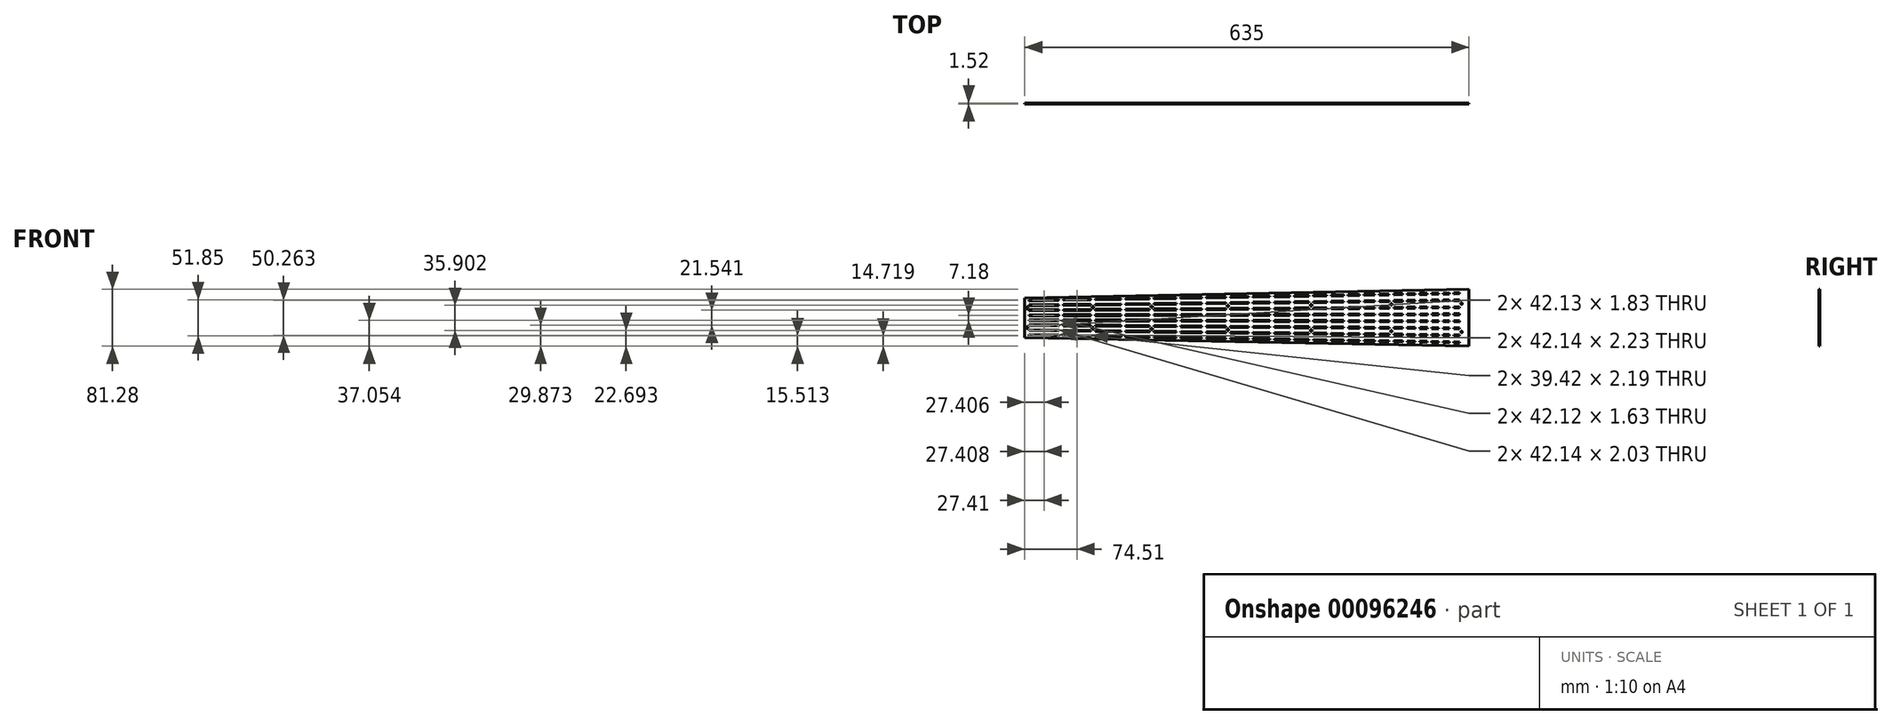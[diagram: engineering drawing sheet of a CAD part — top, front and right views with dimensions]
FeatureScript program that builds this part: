
annotation { "Feature Type Name" : "Feature", "Feature Type Description" : "" }
export const myFeature = defineFeature(function(context is Context, id is Id, definition is map)
    precondition{}
    {
        {
            var Q0;
            Q0=qCreatedBy(makeId("Front.planeOp"),FACE);
            var sketch = newSketch(context, id + "F0", { "sketchPlane" : qUnion([Q0])});
            skLineSegment(sketch, "E0", {"start": v(0, 3.52) * mm, "end": v(646.57, -7.37) * mm, "construction": true});
            skLineSegment(sketch, "E1", {"start": v(0, 4.29) * mm, "end": v(642.9, -6.54) * mm, "construction": true});
            skLineSegment(sketch, "E2", {"start": v(6.35, 3.42) * mm, "end": v(6.36, 4.18) * mm});
            skLineSegment(sketch, "E3", {"start": v(6.36, 4.18) * mm, "end": v(48.48, 3.47) * mm});
            skLineSegment(sketch, "E4", {"start": v(48.48, 3.47) * mm, "end": v(48.46, 2.7) * mm});
            skLineSegment(sketch, "E5", {"start": v(54.81, 2.6) * mm, "end": v(54.83, 3.36) * mm});
            skLineSegment(sketch, "E6", {"start": v(54.83, 3.36) * mm, "end": v(94.22, 2.7) * mm});
            skLineSegment(sketch, "E7", {"start": v(94.22, 2.7) * mm, "end": v(94.2, 1.94) * mm});
            skLineSegment(sketch, "E8", {"start": v(100.56, 1.83) * mm, "end": v(100.57, 2.6) * mm});
            skLineSegment(sketch, "E9", {"start": v(100.57, 2.6) * mm, "end": v(137.4, 1.97) * mm});
            skLineSegment(sketch, "E10", {"start": v(137.4, 1.97) * mm, "end": v(137.38, 1.21) * mm});
            skLineSegment(sketch, "E11", {"start": v(143.73, 1.1) * mm, "end": v(143.74, 1.87) * mm});
            skLineSegment(sketch, "E12", {"start": v(143.74, 1.87) * mm, "end": v(178.14, 1.29) * mm});
            skLineSegment(sketch, "E13", {"start": v(178.14, 1.29) * mm, "end": v(178.13, 0.52) * mm});
            skLineSegment(sketch, "E14", {"start": v(184.48, 0.42) * mm, "end": v(184.49, 1.18) * mm});
            skLineSegment(sketch, "E15", {"start": v(184.49, 1.18) * mm, "end": v(216.61, 0.64) * mm, "construction": true});
            skLineSegment(sketch, "E16", {"start": v(216.61, 0.64) * mm, "end": v(216.6, -0.12) * mm});
            skLineSegment(sketch, "E17", {"start": v(222.95, -0.23) * mm, "end": v(222.96, 0.53) * mm});
            skLineSegment(sketch, "E18", {"start": v(222.96, 0.53) * mm, "end": v(252.92, 0.03) * mm});
            skLineSegment(sketch, "E19", {"start": v(252.92, 0.03) * mm, "end": v(252.9, -0.74) * mm});
            skLineSegment(sketch, "E20", {"start": v(259.26, -0.84) * mm, "end": v(259.27, -0.08) * mm});
            skLineSegment(sketch, "E21", {"start": v(259.27, -0.08) * mm, "end": v(287.19, -0.55) * mm});
            skLineSegment(sketch, "E22", {"start": v(287.19, -0.55) * mm, "end": v(287.18, -1.31) * mm});
            skLineSegment(sketch, "E23", {"start": v(293.52, -1.42) * mm, "end": v(293.54, -0.66) * mm});
            skLineSegment(sketch, "E24", {"start": v(293.54, -0.66) * mm, "end": v(319.53, -1.1) * mm});
            skLineSegment(sketch, "E25", {"start": v(319.53, -1.1) * mm, "end": v(319.52, -1.86) * mm});
            skLineSegment(sketch, "E26", {"start": v(325.87, -1.96) * mm, "end": v(325.88, -1.2) * mm});
            skLineSegment(sketch, "E27", {"start": v(325.88, -1.2) * mm, "end": v(350.06, -1.6) * mm});
            skLineSegment(sketch, "E28", {"start": v(350.06, -1.6) * mm, "end": v(350.05, -2.37) * mm});
            skLineSegment(sketch, "E29", {"start": v(184.49, 1.18) * mm, "end": v(216.61, 0.64) * mm});
            skLineSegment(sketch, "E30", {"start": v(356.4, -2.48) * mm, "end": v(356.41, -1.72) * mm});
            skLineSegment(sketch, "E31", {"start": v(356.41, -1.72) * mm, "end": v(378.88, -2.1) * mm});
            skLineSegment(sketch, "E32", {"start": v(378.88, -2.1) * mm, "end": v(378.87, -2.86) * mm});
            skLineSegment(sketch, "E33", {"start": v(385.22, -2.96) * mm, "end": v(385.23, -2.2) * mm});
            skLineSegment(sketch, "E34", {"start": v(385.23, -2.2) * mm, "end": v(406.08, -2.55) * mm});
            skLineSegment(sketch, "E35", {"start": v(406.08, -2.55) * mm, "end": v(406.07, -3.32) * mm});
            skLineSegment(sketch, "E36", {"start": v(412.41, -3.42) * mm, "end": v(412.43, -2.66) * mm});
            skLineSegment(sketch, "E37", {"start": v(412.43, -2.66) * mm, "end": v(431.75, -2.99) * mm});
            skLineSegment(sketch, "E38", {"start": v(431.75, -2.99) * mm, "end": v(431.74, -3.75) * mm});
            skLineSegment(sketch, "E39", {"start": v(438.09, -3.85) * mm, "end": v(438.1, -3.1) * mm});
            skLineSegment(sketch, "E40", {"start": v(438.1, -3.1) * mm, "end": v(455.98, -3.4) * mm});
            skLineSegment(sketch, "E41", {"start": v(455.98, -3.4) * mm, "end": v(455.97, -4.16) * mm});
            skLineSegment(sketch, "E42", {"start": v(462.32, -4.26) * mm, "end": v(462.33, -3.5) * mm});
            skLineSegment(sketch, "E43", {"start": v(462.33, -3.5) * mm, "end": v(478.86, -3.78) * mm});
            skLineSegment(sketch, "E44", {"start": v(478.86, -3.78) * mm, "end": v(478.84, -4.54) * mm});
            skLineSegment(sketch, "E45", {"start": v(485.2, -4.65) * mm, "end": v(485.2, -3.89) * mm});
            skLineSegment(sketch, "E46", {"start": v(485.2, -3.89) * mm, "end": v(500.44, -4.14) * mm});
            skLineSegment(sketch, "E47", {"start": v(500.44, -4.14) * mm, "end": v(500.43, -4.9) * mm});
            skLineSegment(sketch, "E48", {"start": v(506.78, -5.01) * mm, "end": v(506.8, -4.25) * mm});
            skLineSegment(sketch, "E49", {"start": v(506.8, -4.25) * mm, "end": v(520.82, -4.49) * mm});
            skLineSegment(sketch, "E50", {"start": v(520.82, -4.49) * mm, "end": v(520.8, -5.25) * mm});
            skLineSegment(sketch, "E51", {"start": v(527.16, -5.35) * mm, "end": v(527.17, -4.6) * mm});
            skLineSegment(sketch, "E52", {"start": v(527.17, -4.6) * mm, "end": v(540.05, -4.8) * mm});
            skLineSegment(sketch, "E53", {"start": v(540.05, -4.8) * mm, "end": v(540.04, -5.57) * mm});
            skLineSegment(sketch, "E54", {"start": v(546.39, -5.68) * mm, "end": v(546.4, -4.92) * mm});
            skLineSegment(sketch, "E55", {"start": v(546.4, -4.92) * mm, "end": v(558.2, -5.12) * mm});
            skLineSegment(sketch, "E56", {"start": v(558.2, -5.12) * mm, "end": v(558.2, -5.88) * mm});
            skLineSegment(sketch, "E57", {"start": v(564.54, -5.98) * mm, "end": v(564.55, -5.22) * mm});
            skLineSegment(sketch, "E58", {"start": v(564.55, -5.22) * mm, "end": v(575.34, -5.4) * mm});
            skLineSegment(sketch, "E59", {"start": v(575.34, -5.4) * mm, "end": v(575.33, -6.17) * mm});
            skLineSegment(sketch, "E60", {"start": v(581.68, -6.27) * mm, "end": v(581.69, -5.51) * mm});
            skLineSegment(sketch, "E61", {"start": v(581.69, -5.51) * mm, "end": v(591.51, -5.68) * mm});
            skLineSegment(sketch, "E62", {"start": v(591.51, -5.68) * mm, "end": v(591.5, -6.44) * mm});
            skLineSegment(sketch, "E63", {"start": v(597.85, -6.55) * mm, "end": v(597.86, -5.78) * mm});
            skLineSegment(sketch, "E64", {"start": v(597.86, -5.78) * mm, "end": v(606.78, -5.93) * mm});
            skLineSegment(sketch, "E65", {"start": v(606.78, -5.93) * mm, "end": v(606.76, -6.7) * mm});
            skLineSegment(sketch, "E66", {"start": v(613.11, -6.8) * mm, "end": v(613.13, -6.04) * mm});
            skLineSegment(sketch, "E67", {"start": v(613.13, -6.04) * mm, "end": v(621.19, -6.18) * mm});
            skLineSegment(sketch, "E68", {"start": v(621.19, -6.18) * mm, "end": v(621.17, -6.94) * mm});
            skLineSegment(sketch, "E69.MirrorCS", {"start": v(184.48, 0.42) * mm, "end": v(184.46, -0.34) * mm});
            skLineSegment(sketch, "E70.MirrorCS", {"start": v(606.75, -7.46) * mm, "end": v(606.76, -6.7) * mm});
            skLineSegment(sketch, "E71.MirrorCS", {"start": v(222.95, -0.23) * mm, "end": v(222.94, -1) * mm});
            skLineSegment(sketch, "E72.MirrorCS", {"start": v(558.18, -6.64) * mm, "end": v(558.2, -5.88) * mm});
            skLineSegment(sketch, "E73.MirrorCS", {"start": v(216.59, -0.89) * mm, "end": v(216.6, -0.12) * mm});
            skLineSegment(sketch, "E74.MirrorCS", {"start": v(293.52, -1.42) * mm, "end": v(293.51, -2.18) * mm});
            skLineSegment(sketch, "E75.MirrorCS", {"start": v(94.2, 1.18) * mm, "end": v(94.2, 1.94) * mm});
            skLineSegment(sketch, "E76.MirrorCS", {"start": v(48.45, 1.95) * mm, "end": v(48.46, 2.7) * mm});
            skLineSegment(sketch, "E77.MirrorCS", {"start": v(613.11, -6.8) * mm, "end": v(613.1, -7.56) * mm});
            skLineSegment(sketch, "E78.MirrorCS", {"start": v(597.85, -6.55) * mm, "end": v(597.84, -7.3) * mm});
            skLineSegment(sketch, "E79.MirrorCS", {"start": v(325.87, -1.96) * mm, "end": v(325.86, -2.73) * mm});
            skLineSegment(sketch, "E80.MirrorCS", {"start": v(581.68, -6.27) * mm, "end": v(581.66, -7.03) * mm});
            skLineSegment(sketch, "E81.MirrorCS", {"start": v(478.83, -5.3) * mm, "end": v(478.84, -4.54) * mm});
            skLineSegment(sketch, "E82.MirrorCS", {"start": v(406.05, -4.08) * mm, "end": v(406.07, -3.32) * mm});
            skLineSegment(sketch, "E83.MirrorCS", {"start": v(591.49, -7.2) * mm, "end": v(591.5, -6.44) * mm});
            skLineSegment(sketch, "E84.MirrorCS", {"start": v(485.2, -4.65) * mm, "end": v(485.18, -5.4) * mm});
            skLineSegment(sketch, "E85.MirrorCS", {"start": v(581.66, -7.03) * mm, "end": v(591.49, -7.2) * mm});
            skLineSegment(sketch, "E86.MirrorCS", {"start": v(520.8, -6) * mm, "end": v(520.8, -5.25) * mm});
            skLineSegment(sketch, "E87.MirrorCS", {"start": v(319.5, -2.62) * mm, "end": v(319.52, -1.86) * mm});
            skLineSegment(sketch, "E88.MirrorCS", {"start": v(455.96, -4.92) * mm, "end": v(455.97, -4.16) * mm});
            skLineSegment(sketch, "E89.MirrorCS", {"start": v(564.54, -5.98) * mm, "end": v(564.53, -6.75) * mm});
            skLineSegment(sketch, "E90.MirrorCS", {"start": v(385.22, -2.96) * mm, "end": v(385.2, -3.73) * mm});
            skLineSegment(sketch, "E91.MirrorCS", {"start": v(378.85, -3.62) * mm, "end": v(378.87, -2.86) * mm});
            skLineSegment(sketch, "E92.MirrorCS", {"start": v(506.78, -5.01) * mm, "end": v(506.77, -5.77) * mm});
            skLineSegment(sketch, "E93.MirrorCS", {"start": v(597.84, -7.3) * mm, "end": v(606.75, -7.46) * mm});
            skLineSegment(sketch, "E94.MirrorCS", {"start": v(546.37, -6.44) * mm, "end": v(558.18, -6.64) * mm});
            skLineSegment(sketch, "E95.MirrorCS", {"start": v(143.73, 1.1) * mm, "end": v(143.72, 0.34) * mm});
            skLineSegment(sketch, "E96.MirrorCS", {"start": v(137.37, 0.45) * mm, "end": v(137.38, 1.21) * mm});
            skLineSegment(sketch, "E97.MirrorCS", {"start": v(100.56, 1.83) * mm, "end": v(100.54, 1.07) * mm});
            skLineSegment(sketch, "E98.MirrorCS", {"start": v(54.81, 2.6) * mm, "end": v(54.8, 1.84) * mm});
            skLineSegment(sketch, "E99.MirrorCS", {"start": v(6.35, 3.42) * mm, "end": v(6.34, 2.66) * mm});
            skLineSegment(sketch, "E100.MirrorCS", {"start": v(178.11, -0.24) * mm, "end": v(178.13, 0.52) * mm});
            skLineSegment(sketch, "E101.MirrorCS", {"start": v(431.73, -4.5) * mm, "end": v(431.74, -3.75) * mm});
            skLineSegment(sketch, "E102.MirrorCS", {"start": v(546.39, -5.68) * mm, "end": v(546.37, -6.44) * mm});
            skLineSegment(sketch, "E103.MirrorCS", {"start": v(500.42, -5.67) * mm, "end": v(500.43, -4.9) * mm});
            skLineSegment(sketch, "E104.MirrorCS", {"start": v(287.16, -2.07) * mm, "end": v(287.18, -1.31) * mm});
            skLineSegment(sketch, "E105.MirrorCS", {"start": v(564.53, -6.75) * mm, "end": v(575.31, -6.93) * mm});
            skLineSegment(sketch, "E106.MirrorCS", {"start": v(252.9, -1.5) * mm, "end": v(252.9, -0.74) * mm});
            skLineSegment(sketch, "E107.MirrorCS", {"start": v(613.1, -7.56) * mm, "end": v(621.16, -7.7) * mm});
            skLineSegment(sketch, "E108.MirrorCS", {"start": v(527.16, -5.35) * mm, "end": v(527.14, -6.12) * mm});
            skLineSegment(sketch, "E109.MirrorCS", {"start": v(350.04, -3.13) * mm, "end": v(350.05, -2.37) * mm});
            skLineSegment(sketch, "E110.MirrorCS", {"start": v(412.41, -3.42) * mm, "end": v(412.4, -4.18) * mm});
            skLineSegment(sketch, "E111.MirrorCS", {"start": v(575.31, -6.93) * mm, "end": v(575.33, -6.17) * mm});
            skLineSegment(sketch, "E112.MirrorCS", {"start": v(259.26, -0.84) * mm, "end": v(259.24, -1.6) * mm});
            skLineSegment(sketch, "E113.MirrorCS", {"start": v(621.16, -7.7) * mm, "end": v(621.17, -6.94) * mm});
            skLineSegment(sketch, "E114.MirrorCS", {"start": v(356.4, -2.48) * mm, "end": v(356.39, -3.24) * mm});
            skLineSegment(sketch, "E115.MirrorCS", {"start": v(506.77, -5.77) * mm, "end": v(520.8, -6) * mm});
            skLineSegment(sketch, "E116.MirrorCS", {"start": v(438.09, -3.85) * mm, "end": v(438.08, -4.62) * mm});
            skLineSegment(sketch, "E117.MirrorCS", {"start": v(184.46, -0.34) * mm, "end": v(216.59, -0.89) * mm, "construction": true});
            skLineSegment(sketch, "E118.MirrorCS", {"start": v(462.32, -4.26) * mm, "end": v(462.3, -5.02) * mm});
            skLineSegment(sketch, "E119.MirrorCS", {"start": v(540.03, -6.33) * mm, "end": v(540.04, -5.57) * mm});
            skLineSegment(sketch, "E120.MirrorCS", {"start": v(527.14, -6.12) * mm, "end": v(540.03, -6.33) * mm});
            skLineSegment(sketch, "E121.MirrorCS", {"start": v(222.94, -1) * mm, "end": v(252.9, -1.5) * mm});
            skLineSegment(sketch, "E122.MirrorCS", {"start": v(385.2, -3.73) * mm, "end": v(406.05, -4.08) * mm});
            skLineSegment(sketch, "E123.MirrorCS", {"start": v(293.51, -2.18) * mm, "end": v(319.5, -2.62) * mm});
            skLineSegment(sketch, "E124.MirrorCS", {"start": v(438.08, -4.62) * mm, "end": v(455.96, -4.92) * mm});
            skLineSegment(sketch, "E125.MirrorCS", {"start": v(143.72, 0.34) * mm, "end": v(178.11, -0.24) * mm});
            skLineSegment(sketch, "E126.MirrorCS", {"start": v(54.8, 1.84) * mm, "end": v(94.2, 1.18) * mm});
            skLineSegment(sketch, "E127.MirrorCS", {"start": v(6.34, 2.66) * mm, "end": v(48.45, 1.95) * mm});
            skLineSegment(sketch, "E128.MirrorCS", {"start": v(356.39, -3.24) * mm, "end": v(378.85, -3.62) * mm});
            skLineSegment(sketch, "E129.MirrorCS", {"start": v(259.24, -1.6) * mm, "end": v(287.16, -2.07) * mm});
            skLineSegment(sketch, "E130.MirrorCS", {"start": v(485.18, -5.4) * mm, "end": v(500.42, -5.67) * mm});
            skLineSegment(sketch, "E131.MirrorCS", {"start": v(412.4, -4.18) * mm, "end": v(431.73, -4.5) * mm});
            skLineSegment(sketch, "E132.MirrorCS", {"start": v(184.46, -0.34) * mm, "end": v(216.59, -0.89) * mm});
            skLineSegment(sketch, "E133.MirrorCS", {"start": v(462.3, -5.02) * mm, "end": v(478.83, -5.3) * mm});
            skLineSegment(sketch, "E134.MirrorCS", {"start": v(325.86, -2.73) * mm, "end": v(350.04, -3.13) * mm});
            skLineSegment(sketch, "E135.MirrorCS", {"start": v(100.54, 1.07) * mm, "end": v(137.37, 0.45) * mm});
            skLineSegment(sketch, "E136", {"start": v(-33.04, 0) * mm, "end": v(118.54, 0) * mm, "construction": true});
            skLineSegment(sketch, "E137", {"start": v(0, 10.57) * mm, "end": v(646.61, 2.8) * mm, "construction": true});
            skLineSegment(sketch, "E138", {"start": v(0, 11.33) * mm, "end": v(642.94, 3.6) * mm, "construction": true});
            skLineSegment(sketch, "E139", {"start": v(6.35, 10.5) * mm, "end": v(6.36, 11.26) * mm});
            skLineSegment(sketch, "E140", {"start": v(6.36, 11.26) * mm, "end": v(48.48, 10.75) * mm});
            skLineSegment(sketch, "E141", {"start": v(48.48, 10.75) * mm, "end": v(48.47, 9.99) * mm});
            skLineSegment(sketch, "E142", {"start": v(54.82, 9.91) * mm, "end": v(54.83, 10.68) * mm});
            skLineSegment(sketch, "E143", {"start": v(54.83, 10.68) * mm, "end": v(94.22, 10.2) * mm});
            skLineSegment(sketch, "E144", {"start": v(94.22, 10.2) * mm, "end": v(94.21, 9.44) * mm});
            skLineSegment(sketch, "E145", {"start": v(100.56, 9.36) * mm, "end": v(100.57, 10.12) * mm});
            skLineSegment(sketch, "E146", {"start": v(100.57, 10.12) * mm, "end": v(137.4, 9.68) * mm});
            skLineSegment(sketch, "E147", {"start": v(137.4, 9.68) * mm, "end": v(137.4, 8.92) * mm});
            skLineSegment(sketch, "E148", {"start": v(143.74, 8.84) * mm, "end": v(143.75, 9.6) * mm});
            skLineSegment(sketch, "E149", {"start": v(143.75, 9.6) * mm, "end": v(178.15, 9.2) * mm});
            skLineSegment(sketch, "E150", {"start": v(178.15, 9.2) * mm, "end": v(178.14, 8.43) * mm});
            skLineSegment(sketch, "E151", {"start": v(184.49, 8.35) * mm, "end": v(184.5, 9.12) * mm});
            skLineSegment(sketch, "E152", {"start": v(184.5, 9.12) * mm, "end": v(216.62, 8.73) * mm, "construction": true});
            skLineSegment(sketch, "E153", {"start": v(216.62, 8.73) * mm, "end": v(216.62, 7.97) * mm});
            skLineSegment(sketch, "E154", {"start": v(222.97, 7.9) * mm, "end": v(222.97, 8.65) * mm});
            skLineSegment(sketch, "E155", {"start": v(222.97, 8.65) * mm, "end": v(252.93, 8.3) * mm});
            skLineSegment(sketch, "E156", {"start": v(252.93, 8.3) * mm, "end": v(252.92, 7.53) * mm});
            skLineSegment(sketch, "E157", {"start": v(259.27, 7.45) * mm, "end": v(259.28, 8.22) * mm});
            skLineSegment(sketch, "E158", {"start": v(259.28, 8.22) * mm, "end": v(287.2, 7.88) * mm});
            skLineSegment(sketch, "E159", {"start": v(287.2, 7.88) * mm, "end": v(287.2, 7.12) * mm});
            skLineSegment(sketch, "E160", {"start": v(293.54, 7.04) * mm, "end": v(293.55, 7.8) * mm});
            skLineSegment(sketch, "E161", {"start": v(293.55, 7.8) * mm, "end": v(319.55, 7.5) * mm});
            skLineSegment(sketch, "E162", {"start": v(319.55, 7.5) * mm, "end": v(319.54, 6.73) * mm});
            skLineSegment(sketch, "E163", {"start": v(325.9, 6.65) * mm, "end": v(325.9, 7.41) * mm});
            skLineSegment(sketch, "E164", {"start": v(325.9, 7.41) * mm, "end": v(350.08, 7.12) * mm});
            skLineSegment(sketch, "E165", {"start": v(350.08, 7.12) * mm, "end": v(350.07, 6.36) * mm});
            skLineSegment(sketch, "E166", {"start": v(184.5, 9.12) * mm, "end": v(216.62, 8.73) * mm});
            skLineSegment(sketch, "E167", {"start": v(356.42, 6.28) * mm, "end": v(356.43, 7.05) * mm});
            skLineSegment(sketch, "E168", {"start": v(356.43, 7.05) * mm, "end": v(378.9, 6.78) * mm});
            skLineSegment(sketch, "E169", {"start": v(378.9, 6.78) * mm, "end": v(378.9, 6.01) * mm});
            skLineSegment(sketch, "E170", {"start": v(385.24, 5.94) * mm, "end": v(385.25, 6.7) * mm});
            skLineSegment(sketch, "E171", {"start": v(385.25, 6.7) * mm, "end": v(406.1, 6.45) * mm});
            skLineSegment(sketch, "E172", {"start": v(406.1, 6.45) * mm, "end": v(406.1, 5.69) * mm});
            skLineSegment(sketch, "E173", {"start": v(412.44, 5.61) * mm, "end": v(412.45, 6.37) * mm});
            skLineSegment(sketch, "E174", {"start": v(412.45, 6.37) * mm, "end": v(431.78, 6.14) * mm});
            skLineSegment(sketch, "E175", {"start": v(431.78, 6.14) * mm, "end": v(431.77, 5.38) * mm});
            skLineSegment(sketch, "E176", {"start": v(438.12, 5.3) * mm, "end": v(438.13, 6.06) * mm});
            skLineSegment(sketch, "E177", {"start": v(438.13, 6.06) * mm, "end": v(456.01, 5.85) * mm});
            skLineSegment(sketch, "E178", {"start": v(456.01, 5.85) * mm, "end": v(456, 5.09) * mm});
            skLineSegment(sketch, "E179", {"start": v(462.35, 5.01) * mm, "end": v(462.36, 5.77) * mm});
            skLineSegment(sketch, "E180", {"start": v(462.36, 5.77) * mm, "end": v(478.88, 5.57) * mm});
            skLineSegment(sketch, "E181", {"start": v(478.88, 5.57) * mm, "end": v(478.88, 4.81) * mm});
            skLineSegment(sketch, "E182", {"start": v(485.23, 4.74) * mm, "end": v(485.23, 5.5) * mm});
            skLineSegment(sketch, "E183", {"start": v(485.23, 5.5) * mm, "end": v(500.47, 5.31) * mm});
            skLineSegment(sketch, "E184", {"start": v(500.47, 5.31) * mm, "end": v(500.46, 4.55) * mm});
            skLineSegment(sketch, "E185", {"start": v(506.81, 4.48) * mm, "end": v(506.82, 5.24) * mm});
            skLineSegment(sketch, "E186", {"start": v(506.82, 5.24) * mm, "end": v(520.85, 5.07) * mm});
            skLineSegment(sketch, "E187", {"start": v(520.85, 5.07) * mm, "end": v(520.84, 4.3) * mm});
            skLineSegment(sketch, "E188", {"start": v(527.2, 4.23) * mm, "end": v(527.2, 5) * mm});
            skLineSegment(sketch, "E189", {"start": v(527.2, 5) * mm, "end": v(540.09, 4.84) * mm});
            skLineSegment(sketch, "E190", {"start": v(540.09, 4.84) * mm, "end": v(540.08, 4.08) * mm});
            skLineSegment(sketch, "E191", {"start": v(546.43, 4) * mm, "end": v(546.43, 4.76) * mm});
            skLineSegment(sketch, "E192", {"start": v(546.43, 4.76) * mm, "end": v(558.24, 4.62) * mm});
            skLineSegment(sketch, "E193", {"start": v(558.24, 4.62) * mm, "end": v(558.23, 3.86) * mm});
            skLineSegment(sketch, "E194", {"start": v(564.58, 3.78) * mm, "end": v(564.59, 4.54) * mm});
            skLineSegment(sketch, "E195", {"start": v(564.59, 4.54) * mm, "end": v(575.38, 4.41) * mm});
            skLineSegment(sketch, "E196", {"start": v(575.38, 4.41) * mm, "end": v(575.37, 3.65) * mm});
            skLineSegment(sketch, "E197", {"start": v(581.72, 3.57) * mm, "end": v(581.73, 4.34) * mm});
            skLineSegment(sketch, "E198", {"start": v(581.73, 4.34) * mm, "end": v(591.55, 4.22) * mm});
            skLineSegment(sketch, "E199", {"start": v(591.55, 4.22) * mm, "end": v(591.54, 3.46) * mm});
            skLineSegment(sketch, "E200", {"start": v(597.9, 3.38) * mm, "end": v(597.9, 4.14) * mm});
            skLineSegment(sketch, "E201", {"start": v(597.9, 4.14) * mm, "end": v(606.82, 4.03) * mm});
            skLineSegment(sketch, "E202", {"start": v(606.82, 4.03) * mm, "end": v(606.8, 3.27) * mm});
            skLineSegment(sketch, "E203", {"start": v(613.16, 3.2) * mm, "end": v(613.16, 3.96) * mm});
            skLineSegment(sketch, "E204", {"start": v(613.16, 3.96) * mm, "end": v(621.23, 3.86) * mm});
            skLineSegment(sketch, "E205", {"start": v(621.23, 3.86) * mm, "end": v(621.22, 3.1) * mm});
            skLineSegment(sketch, "E206.MirrorCS", {"start": v(184.49, 8.35) * mm, "end": v(184.48, 7.6) * mm});
            skLineSegment(sketch, "E207.MirrorCS", {"start": v(606.8, 2.51) * mm, "end": v(606.8, 3.27) * mm});
            skLineSegment(sketch, "E208.MirrorCS", {"start": v(222.97, 7.9) * mm, "end": v(222.96, 7.13) * mm});
            skLineSegment(sketch, "E209.MirrorCS", {"start": v(558.22, 3.1) * mm, "end": v(558.23, 3.86) * mm});
            skLineSegment(sketch, "E210.MirrorCS", {"start": v(216.6, 7.2) * mm, "end": v(216.62, 7.97) * mm});
            skLineSegment(sketch, "E211.MirrorCS", {"start": v(293.54, 7.04) * mm, "end": v(293.54, 6.28) * mm});
            skLineSegment(sketch, "E212.MirrorCS", {"start": v(94.2, 8.68) * mm, "end": v(94.21, 9.44) * mm});
            skLineSegment(sketch, "E213.MirrorCS", {"start": v(48.46, 9.23) * mm, "end": v(48.47, 9.99) * mm});
            skLineSegment(sketch, "E214.MirrorCS", {"start": v(613.16, 3.2) * mm, "end": v(613.15, 2.43) * mm});
            skLineSegment(sketch, "E215.MirrorCS", {"start": v(597.9, 3.38) * mm, "end": v(597.88, 2.62) * mm});
            skLineSegment(sketch, "E216.MirrorCS", {"start": v(325.9, 6.65) * mm, "end": v(325.88, 5.9) * mm});
            skLineSegment(sketch, "E217.MirrorCS", {"start": v(581.72, 3.57) * mm, "end": v(581.7, 2.81) * mm});
            skLineSegment(sketch, "E218.MirrorCS", {"start": v(478.87, 4.05) * mm, "end": v(478.88, 4.81) * mm});
            skLineSegment(sketch, "E219.MirrorCS", {"start": v(406.08, 4.93) * mm, "end": v(406.1, 5.69) * mm});
            skLineSegment(sketch, "E220.MirrorCS", {"start": v(591.53, 2.7) * mm, "end": v(591.54, 3.46) * mm});
            skLineSegment(sketch, "E221.MirrorCS", {"start": v(485.23, 4.74) * mm, "end": v(485.22, 3.97) * mm});
            skLineSegment(sketch, "E222.MirrorCS", {"start": v(581.7, 2.81) * mm, "end": v(591.53, 2.7) * mm});
            skLineSegment(sketch, "E223.MirrorCS", {"start": v(520.83, 3.55) * mm, "end": v(520.84, 4.3) * mm});
            skLineSegment(sketch, "E224.MirrorCS", {"start": v(319.53, 5.97) * mm, "end": v(319.54, 6.73) * mm});
            skLineSegment(sketch, "E225.MirrorCS", {"start": v(456, 4.33) * mm, "end": v(456, 5.09) * mm});
            skLineSegment(sketch, "E226.MirrorCS", {"start": v(564.58, 3.78) * mm, "end": v(564.57, 3.02) * mm});
            skLineSegment(sketch, "E227.MirrorCS", {"start": v(385.24, 5.94) * mm, "end": v(385.23, 5.18) * mm});
            skLineSegment(sketch, "E228.MirrorCS", {"start": v(378.88, 5.25) * mm, "end": v(378.9, 6.01) * mm});
            skLineSegment(sketch, "E229.MirrorCS", {"start": v(506.81, 4.48) * mm, "end": v(506.8, 3.71) * mm});
            skLineSegment(sketch, "E230.MirrorCS", {"start": v(597.88, 2.62) * mm, "end": v(606.8, 2.51) * mm});
            skLineSegment(sketch, "E231.MirrorCS", {"start": v(546.42, 3.24) * mm, "end": v(558.22, 3.1) * mm});
            skLineSegment(sketch, "E232.MirrorCS", {"start": v(143.74, 8.84) * mm, "end": v(143.73, 8.08) * mm});
            skLineSegment(sketch, "E233.MirrorCS", {"start": v(137.38, 8.16) * mm, "end": v(137.4, 8.92) * mm});
            skLineSegment(sketch, "E234.MirrorCS", {"start": v(100.56, 9.36) * mm, "end": v(100.55, 8.6) * mm});
            skLineSegment(sketch, "E235.MirrorCS", {"start": v(54.82, 9.91) * mm, "end": v(54.8, 9.15) * mm});
            skLineSegment(sketch, "E236.MirrorCS", {"start": v(6.35, 10.5) * mm, "end": v(6.34, 9.73) * mm});
            skLineSegment(sketch, "E237.MirrorCS", {"start": v(178.13, 7.67) * mm, "end": v(178.14, 8.43) * mm});
            skLineSegment(sketch, "E238.MirrorCS", {"start": v(431.76, 4.62) * mm, "end": v(431.77, 5.38) * mm});
            skLineSegment(sketch, "E239.MirrorCS", {"start": v(546.43, 4) * mm, "end": v(546.42, 3.24) * mm});
            skLineSegment(sketch, "E240.MirrorCS", {"start": v(500.46, 3.8) * mm, "end": v(500.46, 4.55) * mm});
            skLineSegment(sketch, "E241.MirrorCS", {"start": v(287.19, 6.36) * mm, "end": v(287.2, 7.12) * mm});
            skLineSegment(sketch, "E242.MirrorCS", {"start": v(564.57, 3.02) * mm, "end": v(575.36, 2.89) * mm});
            skLineSegment(sketch, "E243.MirrorCS", {"start": v(252.91, 6.77) * mm, "end": v(252.92, 7.53) * mm});
            skLineSegment(sketch, "E244.MirrorCS", {"start": v(613.15, 2.43) * mm, "end": v(621.2, 2.34) * mm});
            skLineSegment(sketch, "E245.MirrorCS", {"start": v(527.2, 4.23) * mm, "end": v(527.18, 3.47) * mm});
            skLineSegment(sketch, "E246.MirrorCS", {"start": v(350.07, 5.6) * mm, "end": v(350.07, 6.36) * mm});
            skLineSegment(sketch, "E247.MirrorCS", {"start": v(412.44, 5.61) * mm, "end": v(412.43, 4.85) * mm});
            skLineSegment(sketch, "E248.MirrorCS", {"start": v(575.36, 2.89) * mm, "end": v(575.37, 3.65) * mm});
            skLineSegment(sketch, "E249.MirrorCS", {"start": v(259.27, 7.45) * mm, "end": v(259.26, 6.7) * mm});
            skLineSegment(sketch, "E250.MirrorCS", {"start": v(621.2, 2.34) * mm, "end": v(621.22, 3.1) * mm});
            skLineSegment(sketch, "E251.MirrorCS", {"start": v(356.42, 6.28) * mm, "end": v(356.42, 5.52) * mm});
            skLineSegment(sketch, "E252.MirrorCS", {"start": v(506.8, 3.71) * mm, "end": v(520.83, 3.55) * mm});
            skLineSegment(sketch, "E253.MirrorCS", {"start": v(438.12, 5.3) * mm, "end": v(438.1, 4.54) * mm});
            skLineSegment(sketch, "E254.MirrorCS", {"start": v(184.48, 7.6) * mm, "end": v(216.6, 7.2) * mm, "construction": true});
            skLineSegment(sketch, "E255.MirrorCS", {"start": v(462.35, 5.01) * mm, "end": v(462.34, 4.25) * mm});
            skLineSegment(sketch, "E256.MirrorCS", {"start": v(540.07, 3.31) * mm, "end": v(540.08, 4.08) * mm});
            skLineSegment(sketch, "E257.MirrorCS", {"start": v(527.18, 3.47) * mm, "end": v(540.07, 3.31) * mm});
            skLineSegment(sketch, "E258.MirrorCS", {"start": v(222.96, 7.13) * mm, "end": v(252.91, 6.77) * mm});
            skLineSegment(sketch, "E259.MirrorCS", {"start": v(385.23, 5.18) * mm, "end": v(406.08, 4.93) * mm});
            skLineSegment(sketch, "E260.MirrorCS", {"start": v(293.54, 6.28) * mm, "end": v(319.53, 5.97) * mm});
            skLineSegment(sketch, "E261.MirrorCS", {"start": v(438.1, 4.54) * mm, "end": v(456, 4.33) * mm});
            skLineSegment(sketch, "E262.MirrorCS", {"start": v(143.73, 8.08) * mm, "end": v(178.13, 7.67) * mm});
            skLineSegment(sketch, "E263.MirrorCS", {"start": v(54.8, 9.15) * mm, "end": v(94.2, 8.68) * mm});
            skLineSegment(sketch, "E264.MirrorCS", {"start": v(6.34, 9.73) * mm, "end": v(48.46, 9.23) * mm});
            skLineSegment(sketch, "E265.MirrorCS", {"start": v(356.42, 5.52) * mm, "end": v(378.88, 5.25) * mm});
            skLineSegment(sketch, "E266.MirrorCS", {"start": v(259.26, 6.7) * mm, "end": v(287.19, 6.36) * mm});
            skLineSegment(sketch, "E267.MirrorCS", {"start": v(485.22, 3.97) * mm, "end": v(500.46, 3.8) * mm});
            skLineSegment(sketch, "E268.MirrorCS", {"start": v(412.43, 4.85) * mm, "end": v(431.76, 4.62) * mm});
            skLineSegment(sketch, "E269.MirrorCS", {"start": v(184.48, 7.6) * mm, "end": v(216.6, 7.2) * mm});
            skLineSegment(sketch, "E270.MirrorCS", {"start": v(462.34, 4.25) * mm, "end": v(478.87, 4.05) * mm});
            skLineSegment(sketch, "E271.MirrorCS", {"start": v(325.88, 5.9) * mm, "end": v(350.07, 5.6) * mm});
            skLineSegment(sketch, "E272.MirrorCS", {"start": v(100.55, 8.6) * mm, "end": v(137.38, 8.16) * mm});
            skLineSegment(sketch, "E273", {"start": v(0, 17.62) * mm, "end": v(646.64, 12.95) * mm, "construction": true});
            skLineSegment(sketch, "E274", {"start": v(0, 18.38) * mm, "end": v(642.97, 13.74) * mm, "construction": true});
            skLineSegment(sketch, "E275", {"start": v(6.35, 17.58) * mm, "end": v(6.36, 18.34) * mm});
            skLineSegment(sketch, "E276", {"start": v(6.36, 18.34) * mm, "end": v(48.47, 18.03) * mm});
            skLineSegment(sketch, "E277", {"start": v(48.47, 18.03) * mm, "end": v(48.47, 17.27) * mm});
            skLineSegment(sketch, "E278", {"start": v(54.82, 17.23) * mm, "end": v(54.82, 17.99) * mm});
            skLineSegment(sketch, "E279", {"start": v(54.82, 17.99) * mm, "end": v(94.22, 17.7) * mm});
            skLineSegment(sketch, "E280", {"start": v(94.22, 17.7) * mm, "end": v(94.22, 16.94) * mm});
            skLineSegment(sketch, "E281", {"start": v(100.57, 16.9) * mm, "end": v(100.57, 17.66) * mm});
            skLineSegment(sketch, "E282", {"start": v(100.57, 17.66) * mm, "end": v(137.4, 17.4) * mm});
            skLineSegment(sketch, "E283", {"start": v(137.4, 17.4) * mm, "end": v(137.4, 16.63) * mm});
            skLineSegment(sketch, "E284", {"start": v(143.75, 16.58) * mm, "end": v(143.75, 17.35) * mm});
            skLineSegment(sketch, "E285", {"start": v(143.75, 17.35) * mm, "end": v(178.15, 17.1) * mm});
            skLineSegment(sketch, "E286", {"start": v(178.15, 17.1) * mm, "end": v(178.15, 16.34) * mm});
            skLineSegment(sketch, "E287", {"start": v(184.5, 16.29) * mm, "end": v(184.5, 17.05) * mm});
            skLineSegment(sketch, "E288", {"start": v(184.5, 17.05) * mm, "end": v(216.63, 16.82) * mm, "construction": true});
            skLineSegment(sketch, "E289", {"start": v(216.63, 16.82) * mm, "end": v(216.63, 16.06) * mm});
            skLineSegment(sketch, "E290", {"start": v(222.98, 16.01) * mm, "end": v(222.98, 16.77) * mm});
            skLineSegment(sketch, "E291", {"start": v(222.98, 16.77) * mm, "end": v(252.94, 16.56) * mm});
            skLineSegment(sketch, "E292", {"start": v(252.94, 16.56) * mm, "end": v(252.94, 15.8) * mm});
            skLineSegment(sketch, "E293", {"start": v(259.29, 15.75) * mm, "end": v(259.3, 16.51) * mm});
            skLineSegment(sketch, "E294", {"start": v(259.3, 16.51) * mm, "end": v(287.21, 16.31) * mm});
            skLineSegment(sketch, "E295", {"start": v(287.21, 16.31) * mm, "end": v(287.2, 15.55) * mm});
            skLineSegment(sketch, "E296", {"start": v(293.56, 15.5) * mm, "end": v(293.56, 16.26) * mm});
            skLineSegment(sketch, "E297", {"start": v(293.56, 16.26) * mm, "end": v(319.56, 16.08) * mm});
            skLineSegment(sketch, "E298", {"start": v(319.56, 16.08) * mm, "end": v(319.56, 15.31) * mm});
            skLineSegment(sketch, "E299", {"start": v(325.9, 15.27) * mm, "end": v(325.91, 16.03) * mm});
            skLineSegment(sketch, "E300", {"start": v(325.91, 16.03) * mm, "end": v(350.1, 15.86) * mm});
            skLineSegment(sketch, "E301", {"start": v(350.1, 15.86) * mm, "end": v(350.1, 15.1) * mm});
            skLineSegment(sketch, "E302", {"start": v(184.5, 17.05) * mm, "end": v(216.63, 16.82) * mm});
            skLineSegment(sketch, "E303", {"start": v(356.44, 15.05) * mm, "end": v(356.45, 15.81) * mm});
            skLineSegment(sketch, "E304", {"start": v(356.45, 15.81) * mm, "end": v(378.92, 15.65) * mm});
            skLineSegment(sketch, "E305", {"start": v(378.92, 15.65) * mm, "end": v(378.91, 14.89) * mm});
            skLineSegment(sketch, "E306", {"start": v(385.26, 14.84) * mm, "end": v(385.27, 15.6) * mm});
            skLineSegment(sketch, "E307", {"start": v(385.27, 15.6) * mm, "end": v(406.12, 15.45) * mm});
            skLineSegment(sketch, "E308", {"start": v(406.12, 15.45) * mm, "end": v(406.11, 14.7) * mm});
            skLineSegment(sketch, "E309", {"start": v(412.46, 14.64) * mm, "end": v(412.47, 15.4) * mm});
            skLineSegment(sketch, "E310", {"start": v(412.47, 15.4) * mm, "end": v(431.8, 15.27) * mm});
            skLineSegment(sketch, "E311", {"start": v(431.8, 15.27) * mm, "end": v(431.79, 14.5) * mm});
            skLineSegment(sketch, "E312", {"start": v(438.14, 14.46) * mm, "end": v(438.14, 15.22) * mm});
            skLineSegment(sketch, "E313", {"start": v(438.14, 15.22) * mm, "end": v(456.03, 15.1) * mm});
            skLineSegment(sketch, "E314", {"start": v(456.03, 15.1) * mm, "end": v(456.02, 14.33) * mm});
            skLineSegment(sketch, "E315", {"start": v(462.37, 14.28) * mm, "end": v(462.38, 15.05) * mm});
            skLineSegment(sketch, "E316", {"start": v(462.38, 15.05) * mm, "end": v(478.9, 14.93) * mm});
            skLineSegment(sketch, "E317", {"start": v(478.9, 14.93) * mm, "end": v(478.9, 14.16) * mm});
            skLineSegment(sketch, "E318", {"start": v(485.25, 14.12) * mm, "end": v(485.25, 14.88) * mm});
            skLineSegment(sketch, "E319", {"start": v(485.25, 14.88) * mm, "end": v(500.5, 14.77) * mm});
            skLineSegment(sketch, "E320", {"start": v(500.5, 14.77) * mm, "end": v(500.49, 14) * mm});
            skLineSegment(sketch, "E321", {"start": v(506.84, 13.96) * mm, "end": v(506.84, 14.73) * mm});
            skLineSegment(sketch, "E322", {"start": v(506.84, 14.73) * mm, "end": v(520.87, 14.62) * mm});
            skLineSegment(sketch, "E323", {"start": v(520.87, 14.62) * mm, "end": v(520.87, 13.86) * mm});
            skLineSegment(sketch, "E324", {"start": v(527.22, 13.82) * mm, "end": v(527.22, 14.58) * mm});
            skLineSegment(sketch, "E325", {"start": v(527.22, 14.58) * mm, "end": v(540.1, 14.48) * mm});
            skLineSegment(sketch, "E326", {"start": v(540.1, 14.48) * mm, "end": v(540.1, 13.72) * mm});
            skLineSegment(sketch, "E327", {"start": v(546.45, 13.68) * mm, "end": v(546.46, 14.44) * mm});
            skLineSegment(sketch, "E328", {"start": v(546.46, 14.44) * mm, "end": v(558.26, 14.35) * mm});
            skLineSegment(sketch, "E329", {"start": v(558.26, 14.35) * mm, "end": v(558.26, 13.6) * mm});
            skLineSegment(sketch, "E330", {"start": v(564.6, 13.55) * mm, "end": v(564.61, 14.3) * mm});
            skLineSegment(sketch, "E331", {"start": v(564.61, 14.3) * mm, "end": v(575.4, 14.23) * mm});
            skLineSegment(sketch, "E332", {"start": v(575.4, 14.23) * mm, "end": v(575.4, 13.47) * mm});
            skLineSegment(sketch, "E333", {"start": v(581.74, 13.42) * mm, "end": v(581.75, 14.18) * mm});
            skLineSegment(sketch, "E334", {"start": v(581.75, 14.18) * mm, "end": v(591.57, 14.11) * mm});
            skLineSegment(sketch, "E335", {"start": v(591.57, 14.11) * mm, "end": v(591.57, 13.35) * mm});
            skLineSegment(sketch, "E336", {"start": v(597.92, 13.3) * mm, "end": v(597.92, 14.07) * mm});
            skLineSegment(sketch, "E337", {"start": v(597.92, 14.07) * mm, "end": v(606.84, 14) * mm});
            skLineSegment(sketch, "E338", {"start": v(606.84, 14) * mm, "end": v(606.83, 13.24) * mm});
            skLineSegment(sketch, "E339", {"start": v(613.18, 13.2) * mm, "end": v(613.19, 13.96) * mm});
            skLineSegment(sketch, "E340", {"start": v(613.19, 13.96) * mm, "end": v(621.25, 13.9) * mm});
            skLineSegment(sketch, "E341", {"start": v(621.25, 13.9) * mm, "end": v(621.24, 13.14) * mm});
            skLineSegment(sketch, "E342.MirrorCS", {"start": v(184.5, 16.29) * mm, "end": v(184.5, 15.53) * mm});
            skLineSegment(sketch, "E343.MirrorCS", {"start": v(606.83, 12.48) * mm, "end": v(606.83, 13.24) * mm});
            skLineSegment(sketch, "E344.MirrorCS", {"start": v(222.98, 16.01) * mm, "end": v(222.97, 15.25) * mm});
            skLineSegment(sketch, "E345.MirrorCS", {"start": v(558.25, 12.83) * mm, "end": v(558.26, 13.6) * mm});
            skLineSegment(sketch, "E346.MirrorCS", {"start": v(216.62, 15.3) * mm, "end": v(216.63, 16.06) * mm});
            skLineSegment(sketch, "E347.MirrorCS", {"start": v(293.56, 15.5) * mm, "end": v(293.55, 14.74) * mm});
            skLineSegment(sketch, "E348.MirrorCS", {"start": v(94.21, 16.18) * mm, "end": v(94.22, 16.94) * mm});
            skLineSegment(sketch, "E349.MirrorCS", {"start": v(48.46, 16.5) * mm, "end": v(48.47, 17.27) * mm});
            skLineSegment(sketch, "E350.MirrorCS", {"start": v(613.18, 13.2) * mm, "end": v(613.18, 12.43) * mm});
            skLineSegment(sketch, "E351.MirrorCS", {"start": v(597.92, 13.3) * mm, "end": v(597.91, 12.54) * mm});
            skLineSegment(sketch, "E352.MirrorCS", {"start": v(325.9, 15.27) * mm, "end": v(325.9, 14.5) * mm});
            skLineSegment(sketch, "E353.MirrorCS", {"start": v(581.74, 13.42) * mm, "end": v(581.74, 12.66) * mm});
            skLineSegment(sketch, "E354.MirrorCS", {"start": v(478.9, 13.4) * mm, "end": v(478.9, 14.16) * mm});
            skLineSegment(sketch, "E355.MirrorCS", {"start": v(406.1, 13.93) * mm, "end": v(406.11, 14.7) * mm});
            skLineSegment(sketch, "E356.MirrorCS", {"start": v(591.56, 12.59) * mm, "end": v(591.57, 13.35) * mm});
            skLineSegment(sketch, "E357.MirrorCS", {"start": v(485.25, 14.12) * mm, "end": v(485.24, 13.36) * mm});
            skLineSegment(sketch, "E358.MirrorCS", {"start": v(581.74, 12.66) * mm, "end": v(591.56, 12.59) * mm});
            skLineSegment(sketch, "E359.MirrorCS", {"start": v(520.86, 13.1) * mm, "end": v(520.87, 13.86) * mm});
            skLineSegment(sketch, "E360.MirrorCS", {"start": v(319.55, 14.55) * mm, "end": v(319.56, 15.31) * mm});
            skLineSegment(sketch, "E361.MirrorCS", {"start": v(456.02, 13.57) * mm, "end": v(456.02, 14.33) * mm});
            skLineSegment(sketch, "E362.MirrorCS", {"start": v(564.6, 13.55) * mm, "end": v(564.6, 12.78) * mm});
            skLineSegment(sketch, "E363.MirrorCS", {"start": v(385.26, 14.84) * mm, "end": v(385.26, 14.08) * mm});
            skLineSegment(sketch, "E364.MirrorCS", {"start": v(378.9, 14.12) * mm, "end": v(378.91, 14.89) * mm});
            skLineSegment(sketch, "E365.MirrorCS", {"start": v(506.84, 13.96) * mm, "end": v(506.83, 13.2) * mm});
            skLineSegment(sketch, "E366.MirrorCS", {"start": v(597.91, 12.54) * mm, "end": v(606.83, 12.48) * mm});
            skLineSegment(sketch, "E367.MirrorCS", {"start": v(546.45, 12.92) * mm, "end": v(558.25, 12.83) * mm});
            skLineSegment(sketch, "E368.MirrorCS", {"start": v(143.75, 16.58) * mm, "end": v(143.74, 15.82) * mm});
            skLineSegment(sketch, "E369.MirrorCS", {"start": v(137.4, 15.87) * mm, "end": v(137.4, 16.63) * mm});
            skLineSegment(sketch, "E370.MirrorCS", {"start": v(100.57, 16.9) * mm, "end": v(100.56, 16.13) * mm});
            skLineSegment(sketch, "E371.MirrorCS", {"start": v(54.82, 17.23) * mm, "end": v(54.81, 16.46) * mm});
            skLineSegment(sketch, "E372.MirrorCS", {"start": v(6.35, 17.58) * mm, "end": v(6.34, 16.81) * mm});
            skLineSegment(sketch, "E373.MirrorCS", {"start": v(178.14, 15.57) * mm, "end": v(178.15, 16.34) * mm});
            skLineSegment(sketch, "E374.MirrorCS", {"start": v(431.78, 13.74) * mm, "end": v(431.79, 14.5) * mm});
            skLineSegment(sketch, "E375.MirrorCS", {"start": v(546.45, 13.68) * mm, "end": v(546.45, 12.92) * mm});
            skLineSegment(sketch, "E376.MirrorCS", {"start": v(500.48, 13.25) * mm, "end": v(500.49, 14) * mm});
            skLineSegment(sketch, "E377.MirrorCS", {"start": v(287.2, 14.79) * mm, "end": v(287.2, 15.55) * mm});
            skLineSegment(sketch, "E378.MirrorCS", {"start": v(564.6, 12.78) * mm, "end": v(575.39, 12.7) * mm});
            skLineSegment(sketch, "E379.MirrorCS", {"start": v(252.93, 15.03) * mm, "end": v(252.94, 15.8) * mm});
            skLineSegment(sketch, "E380.MirrorCS", {"start": v(613.18, 12.43) * mm, "end": v(621.24, 12.38) * mm});
            skLineSegment(sketch, "E381.MirrorCS", {"start": v(527.22, 13.82) * mm, "end": v(527.21, 13.05) * mm});
            skLineSegment(sketch, "E382.MirrorCS", {"start": v(350.09, 14.33) * mm, "end": v(350.1, 15.1) * mm});
            skLineSegment(sketch, "E383.MirrorCS", {"start": v(412.46, 14.64) * mm, "end": v(412.46, 13.88) * mm});
            skLineSegment(sketch, "E384.MirrorCS", {"start": v(575.39, 12.7) * mm, "end": v(575.4, 13.47) * mm});
            skLineSegment(sketch, "E385.MirrorCS", {"start": v(259.29, 15.75) * mm, "end": v(259.28, 14.99) * mm});
            skLineSegment(sketch, "E386.MirrorCS", {"start": v(621.24, 12.38) * mm, "end": v(621.24, 13.14) * mm});
            skLineSegment(sketch, "E387.MirrorCS", {"start": v(356.44, 15.05) * mm, "end": v(356.44, 14.29) * mm});
            skLineSegment(sketch, "E388.MirrorCS", {"start": v(506.83, 13.2) * mm, "end": v(520.86, 13.1) * mm});
            skLineSegment(sketch, "E389.MirrorCS", {"start": v(438.14, 14.46) * mm, "end": v(438.13, 13.7) * mm});
            skLineSegment(sketch, "E390.MirrorCS", {"start": v(184.5, 15.53) * mm, "end": v(216.62, 15.3) * mm, "construction": true});
            skLineSegment(sketch, "E391.MirrorCS", {"start": v(462.37, 14.28) * mm, "end": v(462.37, 13.52) * mm});
            skLineSegment(sketch, "E392.MirrorCS", {"start": v(540.1, 12.96) * mm, "end": v(540.1, 13.72) * mm});
            skLineSegment(sketch, "E393.MirrorCS", {"start": v(527.21, 13.05) * mm, "end": v(540.1, 12.96) * mm});
            skLineSegment(sketch, "E394.MirrorCS", {"start": v(222.97, 15.25) * mm, "end": v(252.93, 15.03) * mm});
            skLineSegment(sketch, "E395.MirrorCS", {"start": v(385.26, 14.08) * mm, "end": v(406.1, 13.93) * mm});
            skLineSegment(sketch, "E396.MirrorCS", {"start": v(293.55, 14.74) * mm, "end": v(319.55, 14.55) * mm});
            skLineSegment(sketch, "E397.MirrorCS", {"start": v(438.13, 13.7) * mm, "end": v(456.02, 13.57) * mm});
            skLineSegment(sketch, "E398.MirrorCS", {"start": v(143.74, 15.82) * mm, "end": v(178.14, 15.57) * mm});
            skLineSegment(sketch, "E399.MirrorCS", {"start": v(54.81, 16.46) * mm, "end": v(94.21, 16.18) * mm});
            skLineSegment(sketch, "E400.MirrorCS", {"start": v(6.34, 16.81) * mm, "end": v(48.46, 16.5) * mm});
            skLineSegment(sketch, "E401.MirrorCS", {"start": v(356.44, 14.29) * mm, "end": v(378.9, 14.12) * mm});
            skLineSegment(sketch, "E402.MirrorCS", {"start": v(259.28, 14.99) * mm, "end": v(287.2, 14.79) * mm});
            skLineSegment(sketch, "E403.MirrorCS", {"start": v(485.24, 13.36) * mm, "end": v(500.48, 13.25) * mm});
            skLineSegment(sketch, "E404.MirrorCS", {"start": v(412.46, 13.88) * mm, "end": v(431.78, 13.74) * mm});
            skLineSegment(sketch, "E405.MirrorCS", {"start": v(184.5, 15.53) * mm, "end": v(216.62, 15.3) * mm});
            skLineSegment(sketch, "E406.MirrorCS", {"start": v(462.37, 13.52) * mm, "end": v(478.9, 13.4) * mm});
            skLineSegment(sketch, "E407.MirrorCS", {"start": v(325.9, 14.5) * mm, "end": v(350.09, 14.33) * mm});
            skLineSegment(sketch, "E408.MirrorCS", {"start": v(100.56, 16.13) * mm, "end": v(137.4, 15.87) * mm});
            skLineSegment(sketch, "E409", {"start": v(0, 24.67) * mm, "end": v(646.66, 23.11) * mm, "construction": true});
            skLineSegment(sketch, "E410", {"start": v(0, 25.43) * mm, "end": v(642.98, 23.88) * mm, "construction": true});
            skLineSegment(sketch, "E411", {"start": v(6.35, 24.65) * mm, "end": v(6.35, 25.42) * mm});
            skLineSegment(sketch, "E412", {"start": v(6.35, 25.42) * mm, "end": v(48.47, 25.32) * mm});
            skLineSegment(sketch, "E413", {"start": v(48.47, 25.32) * mm, "end": v(48.47, 24.55) * mm});
            skLineSegment(sketch, "E414", {"start": v(54.82, 24.54) * mm, "end": v(54.82, 25.3) * mm});
            skLineSegment(sketch, "E415", {"start": v(54.82, 25.3) * mm, "end": v(94.22, 25.2) * mm});
            skLineSegment(sketch, "E416", {"start": v(94.22, 25.2) * mm, "end": v(94.22, 24.44) * mm});
            skLineSegment(sketch, "E417", {"start": v(100.57, 24.43) * mm, "end": v(100.57, 25.19) * mm});
            skLineSegment(sketch, "E418", {"start": v(100.57, 25.19) * mm, "end": v(137.4, 25.1) * mm});
            skLineSegment(sketch, "E419", {"start": v(137.4, 25.1) * mm, "end": v(137.4, 24.34) * mm});
            skLineSegment(sketch, "E420", {"start": v(143.75, 24.32) * mm, "end": v(143.75, 25.09) * mm});
            skLineSegment(sketch, "E421", {"start": v(143.75, 25.09) * mm, "end": v(178.15, 25) * mm});
            skLineSegment(sketch, "E422", {"start": v(178.15, 25) * mm, "end": v(178.15, 24.24) * mm});
            skLineSegment(sketch, "E423", {"start": v(184.5, 24.23) * mm, "end": v(184.5, 24.99) * mm});
            skLineSegment(sketch, "E424", {"start": v(184.5, 24.99) * mm, "end": v(216.63, 24.91) * mm, "construction": true});
            skLineSegment(sketch, "E425", {"start": v(216.63, 24.91) * mm, "end": v(216.63, 24.15) * mm});
            skLineSegment(sketch, "E426", {"start": v(222.98, 24.13) * mm, "end": v(222.98, 24.9) * mm});
            skLineSegment(sketch, "E427", {"start": v(222.98, 24.9) * mm, "end": v(252.94, 24.82) * mm});
            skLineSegment(sketch, "E428", {"start": v(252.94, 24.82) * mm, "end": v(252.94, 24.06) * mm});
            skLineSegment(sketch, "E429", {"start": v(259.3, 24.05) * mm, "end": v(259.3, 24.8) * mm});
            skLineSegment(sketch, "E430", {"start": v(259.3, 24.8) * mm, "end": v(287.22, 24.74) * mm});
            skLineSegment(sketch, "E431", {"start": v(287.22, 24.74) * mm, "end": v(287.22, 23.98) * mm});
            skLineSegment(sketch, "E432", {"start": v(293.57, 23.96) * mm, "end": v(293.57, 24.73) * mm});
            skLineSegment(sketch, "E433", {"start": v(293.57, 24.73) * mm, "end": v(319.57, 24.66) * mm});
            skLineSegment(sketch, "E434", {"start": v(319.57, 24.66) * mm, "end": v(319.56, 23.9) * mm});
            skLineSegment(sketch, "E435", {"start": v(325.91, 23.89) * mm, "end": v(325.92, 24.65) * mm});
            skLineSegment(sketch, "E436", {"start": v(325.92, 24.65) * mm, "end": v(350.1, 24.59) * mm});
            skLineSegment(sketch, "E437", {"start": v(350.1, 24.59) * mm, "end": v(350.1, 23.83) * mm});
            skLineSegment(sketch, "E438", {"start": v(184.5, 24.99) * mm, "end": v(216.63, 24.91) * mm});
            skLineSegment(sketch, "E439", {"start": v(356.45, 23.81) * mm, "end": v(356.45, 24.57) * mm});
            skLineSegment(sketch, "E440", {"start": v(356.45, 24.57) * mm, "end": v(378.92, 24.52) * mm});
            skLineSegment(sketch, "E441", {"start": v(378.92, 24.52) * mm, "end": v(378.92, 23.76) * mm});
            skLineSegment(sketch, "E442", {"start": v(385.27, 23.74) * mm, "end": v(385.27, 24.5) * mm});
            skLineSegment(sketch, "E443", {"start": v(385.27, 24.5) * mm, "end": v(406.12, 24.45) * mm});
            skLineSegment(sketch, "E444", {"start": v(406.12, 24.45) * mm, "end": v(406.12, 23.7) * mm});
            skLineSegment(sketch, "E445", {"start": v(412.47, 23.68) * mm, "end": v(412.47, 24.44) * mm});
            skLineSegment(sketch, "E446", {"start": v(412.47, 24.44) * mm, "end": v(431.8, 24.4) * mm});
            skLineSegment(sketch, "E447", {"start": v(431.8, 24.4) * mm, "end": v(431.8, 23.63) * mm});
            skLineSegment(sketch, "E448", {"start": v(438.15, 23.62) * mm, "end": v(438.15, 24.38) * mm});
            skLineSegment(sketch, "E449", {"start": v(438.15, 24.38) * mm, "end": v(456.04, 24.33) * mm});
            skLineSegment(sketch, "E450", {"start": v(456.04, 24.33) * mm, "end": v(456.03, 23.57) * mm});
            skLineSegment(sketch, "E451", {"start": v(462.38, 23.56) * mm, "end": v(462.39, 24.32) * mm});
            skLineSegment(sketch, "E452", {"start": v(462.39, 24.32) * mm, "end": v(478.91, 24.28) * mm});
            skLineSegment(sketch, "E453", {"start": v(478.91, 24.28) * mm, "end": v(478.9, 23.52) * mm});
            skLineSegment(sketch, "E454", {"start": v(485.26, 23.5) * mm, "end": v(485.26, 24.26) * mm});
            skLineSegment(sketch, "E455", {"start": v(485.26, 24.26) * mm, "end": v(500.5, 24.23) * mm});
            skLineSegment(sketch, "E456", {"start": v(500.5, 24.23) * mm, "end": v(500.5, 23.47) * mm});
            skLineSegment(sketch, "E457", {"start": v(506.85, 23.45) * mm, "end": v(506.85, 24.21) * mm});
            skLineSegment(sketch, "E458", {"start": v(506.85, 24.21) * mm, "end": v(520.88, 24.18) * mm});
            skLineSegment(sketch, "E459", {"start": v(520.88, 24.18) * mm, "end": v(520.88, 23.42) * mm});
            skLineSegment(sketch, "E460", {"start": v(527.23, 23.4) * mm, "end": v(527.23, 24.16) * mm});
            skLineSegment(sketch, "E461", {"start": v(527.23, 24.16) * mm, "end": v(540.12, 24.13) * mm});
            skLineSegment(sketch, "E462", {"start": v(540.12, 24.13) * mm, "end": v(540.11, 23.37) * mm});
            skLineSegment(sketch, "E463", {"start": v(546.46, 23.36) * mm, "end": v(546.47, 24.12) * mm});
            skLineSegment(sketch, "E464", {"start": v(546.47, 24.12) * mm, "end": v(558.27, 24.09) * mm});
            skLineSegment(sketch, "E465", {"start": v(558.27, 24.09) * mm, "end": v(558.27, 23.33) * mm});
            skLineSegment(sketch, "E466", {"start": v(564.62, 23.31) * mm, "end": v(564.62, 24.07) * mm});
            skLineSegment(sketch, "E467", {"start": v(564.62, 24.07) * mm, "end": v(575.4, 24.05) * mm});
            skLineSegment(sketch, "E468", {"start": v(575.4, 24.05) * mm, "end": v(575.4, 23.29) * mm});
            skLineSegment(sketch, "E469", {"start": v(581.76, 23.27) * mm, "end": v(581.76, 24.03) * mm});
            skLineSegment(sketch, "E470", {"start": v(581.76, 24.03) * mm, "end": v(591.58, 24) * mm});
            skLineSegment(sketch, "E471", {"start": v(591.58, 24) * mm, "end": v(591.58, 23.25) * mm});
            skLineSegment(sketch, "E472", {"start": v(597.93, 23.23) * mm, "end": v(597.93, 24) * mm});
            skLineSegment(sketch, "E473", {"start": v(597.93, 24) * mm, "end": v(606.85, 23.97) * mm});
            skLineSegment(sketch, "E474", {"start": v(606.85, 23.97) * mm, "end": v(606.85, 23.2) * mm});
            skLineSegment(sketch, "E475", {"start": v(613.2, 23.2) * mm, "end": v(613.2, 23.96) * mm});
            skLineSegment(sketch, "E476", {"start": v(613.2, 23.96) * mm, "end": v(621.26, 23.94) * mm});
            skLineSegment(sketch, "E477", {"start": v(621.26, 23.94) * mm, "end": v(621.26, 23.18) * mm});
            skLineSegment(sketch, "E478.MirrorCS", {"start": v(184.5, 24.23) * mm, "end": v(184.5, 23.46) * mm});
            skLineSegment(sketch, "E479.MirrorCS", {"start": v(606.85, 22.45) * mm, "end": v(606.85, 23.2) * mm});
            skLineSegment(sketch, "E480.MirrorCS", {"start": v(222.98, 24.13) * mm, "end": v(222.98, 23.37) * mm});
            skLineSegment(sketch, "E481.MirrorCS", {"start": v(558.27, 22.56) * mm, "end": v(558.27, 23.33) * mm});
            skLineSegment(sketch, "E482.MirrorCS", {"start": v(216.63, 23.39) * mm, "end": v(216.63, 24.15) * mm});
            skLineSegment(sketch, "E483.MirrorCS", {"start": v(293.57, 23.96) * mm, "end": v(293.56, 23.2) * mm});
            skLineSegment(sketch, "E484.MirrorCS", {"start": v(94.22, 23.68) * mm, "end": v(94.22, 24.44) * mm});
            skLineSegment(sketch, "E485.MirrorCS", {"start": v(48.47, 23.8) * mm, "end": v(48.47, 24.55) * mm});
            skLineSegment(sketch, "E486.MirrorCS", {"start": v(613.2, 23.2) * mm, "end": v(613.2, 22.43) * mm});
            skLineSegment(sketch, "E487.MirrorCS", {"start": v(597.93, 23.23) * mm, "end": v(597.93, 22.47) * mm});
            skLineSegment(sketch, "E488.MirrorCS", {"start": v(325.91, 23.89) * mm, "end": v(325.91, 23.12) * mm});
            skLineSegment(sketch, "E489.MirrorCS", {"start": v(581.76, 23.27) * mm, "end": v(581.75, 22.5) * mm});
            skLineSegment(sketch, "E490.MirrorCS", {"start": v(478.9, 22.76) * mm, "end": v(478.9, 23.52) * mm});
            skLineSegment(sketch, "E491.MirrorCS", {"start": v(406.12, 22.93) * mm, "end": v(406.12, 23.7) * mm});
            skLineSegment(sketch, "E492.MirrorCS", {"start": v(591.58, 22.48) * mm, "end": v(591.58, 23.25) * mm});
            skLineSegment(sketch, "E493.MirrorCS", {"start": v(485.26, 23.5) * mm, "end": v(485.26, 22.74) * mm});
            skLineSegment(sketch, "E494.MirrorCS", {"start": v(581.75, 22.5) * mm, "end": v(591.58, 22.48) * mm});
            skLineSegment(sketch, "E495.MirrorCS", {"start": v(520.88, 22.65) * mm, "end": v(520.88, 23.42) * mm});
            skLineSegment(sketch, "E496.MirrorCS", {"start": v(319.56, 23.14) * mm, "end": v(319.56, 23.9) * mm});
            skLineSegment(sketch, "E497.MirrorCS", {"start": v(456.03, 22.81) * mm, "end": v(456.03, 23.57) * mm});
            skLineSegment(sketch, "E498.MirrorCS", {"start": v(564.62, 23.31) * mm, "end": v(564.62, 22.55) * mm});
            skLineSegment(sketch, "E499.MirrorCS", {"start": v(385.27, 23.74) * mm, "end": v(385.27, 22.98) * mm});
            skLineSegment(sketch, "E500.MirrorCS", {"start": v(378.92, 23) * mm, "end": v(378.92, 23.76) * mm});
            skLineSegment(sketch, "E501.MirrorCS", {"start": v(506.85, 23.45) * mm, "end": v(506.85, 22.69) * mm});
            skLineSegment(sketch, "E502.MirrorCS", {"start": v(597.93, 22.47) * mm, "end": v(606.85, 22.45) * mm});
            skLineSegment(sketch, "E503.MirrorCS", {"start": v(546.46, 22.6) * mm, "end": v(558.27, 22.56) * mm});
            skLineSegment(sketch, "E504.MirrorCS", {"start": v(143.75, 24.32) * mm, "end": v(143.75, 23.56) * mm});
            skLineSegment(sketch, "E505.MirrorCS", {"start": v(137.4, 23.58) * mm, "end": v(137.4, 24.34) * mm});
            skLineSegment(sketch, "E506.MirrorCS", {"start": v(100.57, 24.43) * mm, "end": v(100.57, 23.67) * mm});
            skLineSegment(sketch, "E507.MirrorCS", {"start": v(54.82, 24.54) * mm, "end": v(54.82, 23.78) * mm});
            skLineSegment(sketch, "E508.MirrorCS", {"start": v(6.35, 24.65) * mm, "end": v(6.35, 23.9) * mm});
            skLineSegment(sketch, "E509.MirrorCS", {"start": v(178.15, 23.48) * mm, "end": v(178.15, 24.24) * mm});
            skLineSegment(sketch, "E510.MirrorCS", {"start": v(431.8, 22.87) * mm, "end": v(431.8, 23.63) * mm});
            skLineSegment(sketch, "E511.MirrorCS", {"start": v(546.46, 23.36) * mm, "end": v(546.46, 22.6) * mm});
            skLineSegment(sketch, "E512.MirrorCS", {"start": v(500.5, 22.7) * mm, "end": v(500.5, 23.47) * mm});
            skLineSegment(sketch, "E513.MirrorCS", {"start": v(287.21, 23.22) * mm, "end": v(287.22, 23.98) * mm});
            skLineSegment(sketch, "E514.MirrorCS", {"start": v(564.62, 22.55) * mm, "end": v(575.4, 22.52) * mm});
            skLineSegment(sketch, "E515.MirrorCS", {"start": v(252.94, 23.3) * mm, "end": v(252.94, 24.06) * mm});
            skLineSegment(sketch, "E516.MirrorCS", {"start": v(613.2, 22.43) * mm, "end": v(621.26, 22.41) * mm});
            skLineSegment(sketch, "E517.MirrorCS", {"start": v(527.23, 23.4) * mm, "end": v(527.23, 22.64) * mm});
            skLineSegment(sketch, "E518.MirrorCS", {"start": v(350.1, 23.07) * mm, "end": v(350.1, 23.83) * mm});
            skLineSegment(sketch, "E519.MirrorCS", {"start": v(412.47, 23.68) * mm, "end": v(412.47, 22.92) * mm});
            skLineSegment(sketch, "E520.MirrorCS", {"start": v(575.4, 22.52) * mm, "end": v(575.4, 23.29) * mm});
            skLineSegment(sketch, "E521.MirrorCS", {"start": v(259.3, 24.05) * mm, "end": v(259.29, 23.28) * mm});
            skLineSegment(sketch, "E522.MirrorCS", {"start": v(621.26, 22.41) * mm, "end": v(621.26, 23.18) * mm});
            skLineSegment(sketch, "E523.MirrorCS", {"start": v(356.45, 23.81) * mm, "end": v(356.45, 23.05) * mm});
            skLineSegment(sketch, "E524.MirrorCS", {"start": v(506.85, 22.69) * mm, "end": v(520.88, 22.65) * mm});
            skLineSegment(sketch, "E525.MirrorCS", {"start": v(438.15, 23.62) * mm, "end": v(438.15, 22.85) * mm});
            skLineSegment(sketch, "E526.MirrorCS", {"start": v(184.5, 23.46) * mm, "end": v(216.63, 23.39) * mm, "construction": true});
            skLineSegment(sketch, "E527.MirrorCS", {"start": v(462.38, 23.56) * mm, "end": v(462.38, 22.8) * mm});
            skLineSegment(sketch, "E528.MirrorCS", {"start": v(540.11, 22.6) * mm, "end": v(540.11, 23.37) * mm});
            skLineSegment(sketch, "E529.MirrorCS", {"start": v(527.23, 22.64) * mm, "end": v(540.11, 22.6) * mm});
            skLineSegment(sketch, "E530.MirrorCS", {"start": v(222.98, 23.37) * mm, "end": v(252.94, 23.3) * mm});
            skLineSegment(sketch, "E531.MirrorCS", {"start": v(385.27, 22.98) * mm, "end": v(406.12, 22.93) * mm});
            skLineSegment(sketch, "E532.MirrorCS", {"start": v(293.56, 23.2) * mm, "end": v(319.56, 23.14) * mm});
            skLineSegment(sketch, "E533.MirrorCS", {"start": v(438.15, 22.85) * mm, "end": v(456.03, 22.81) * mm});
            skLineSegment(sketch, "E534.MirrorCS", {"start": v(143.75, 23.56) * mm, "end": v(178.15, 23.48) * mm});
            skLineSegment(sketch, "E535.MirrorCS", {"start": v(54.82, 23.78) * mm, "end": v(94.22, 23.68) * mm});
            skLineSegment(sketch, "E536.MirrorCS", {"start": v(6.35, 23.9) * mm, "end": v(48.47, 23.8) * mm});
            skLineSegment(sketch, "E537.MirrorCS", {"start": v(356.45, 23.05) * mm, "end": v(378.92, 23) * mm});
            skLineSegment(sketch, "E538.MirrorCS", {"start": v(259.29, 23.28) * mm, "end": v(287.21, 23.22) * mm});
            skLineSegment(sketch, "E539.MirrorCS", {"start": v(485.26, 22.74) * mm, "end": v(500.5, 22.7) * mm});
            skLineSegment(sketch, "E540.MirrorCS", {"start": v(412.47, 22.92) * mm, "end": v(431.8, 22.87) * mm});
            skLineSegment(sketch, "E541.MirrorCS", {"start": v(184.5, 23.46) * mm, "end": v(216.63, 23.39) * mm});
            skLineSegment(sketch, "E542.MirrorCS", {"start": v(462.38, 22.8) * mm, "end": v(478.9, 22.76) * mm});
            skLineSegment(sketch, "E543.MirrorCS", {"start": v(325.91, 23.12) * mm, "end": v(350.1, 23.07) * mm});
            skLineSegment(sketch, "E544.MirrorCS", {"start": v(100.57, 23.67) * mm, "end": v(137.4, 23.58) * mm});
            skLineSegment(sketch, "E545", {"start": v(0, 28.2) * mm, "end": v(665.02, 28.2) * mm, "construction": true});
            skLineSegment(sketch, "E546.MirrorCS", {"start": v(216.62, 41.1) * mm, "end": v(216.63, 40.33) * mm});
            skLineSegment(sketch, "E547.MirrorCS", {"start": v(216.63, 39.57) * mm, "end": v(216.63, 40.33) * mm});
            skLineSegment(sketch, "E548.MirrorCS", {"start": v(184.5, 40.1) * mm, "end": v(184.5, 39.34) * mm});
            skLineSegment(sketch, "E549.MirrorCS", {"start": v(94.2, 55.21) * mm, "end": v(94.2, 54.45) * mm});
            skLineSegment(sketch, "E550.MirrorCS", {"start": v(48.45, 54.44) * mm, "end": v(48.46, 53.68) * mm});
            skLineSegment(sketch, "E551.MirrorCS", {"start": v(184.5, 40.1) * mm, "end": v(184.5, 40.86) * mm});
            skLineSegment(sketch, "E552.MirrorCS", {"start": v(216.62, 47.66) * mm, "end": v(216.62, 48.42) * mm});
            skLineSegment(sketch, "E553.MirrorCS", {"start": v(350.08, 49.26) * mm, "end": v(350.07, 50.03) * mm});
            skLineSegment(sketch, "E554.MirrorCS", {"start": v(356.42, 50.1) * mm, "end": v(356.43, 49.34) * mm});
            skLineSegment(sketch, "E555.MirrorCS", {"start": v(6.35, 38.81) * mm, "end": v(6.36, 38.05) * mm});
            skLineSegment(sketch, "E556.MirrorCS", {"start": v(325.9, 49.74) * mm, "end": v(325.9, 48.97) * mm});
            skLineSegment(sketch, "E557.MirrorCS", {"start": v(216.6, 49.18) * mm, "end": v(216.62, 48.42) * mm});
            skLineSegment(sketch, "E558.MirrorCS", {"start": v(54.81, 53.79) * mm, "end": v(54.8, 54.55) * mm});
            skLineSegment(sketch, "E559.MirrorCS", {"start": v(100.56, 54.56) * mm, "end": v(100.54, 55.32) * mm});
            skLineSegment(sketch, "E560.MirrorCS", {"start": v(325.9, 41.12) * mm, "end": v(325.9, 41.88) * mm});
            skLineSegment(sketch, "E561.MirrorCS", {"start": v(319.53, 50.42) * mm, "end": v(319.54, 49.66) * mm});
            skLineSegment(sketch, "E562.MirrorCS", {"start": v(540.07, 53.07) * mm, "end": v(540.08, 52.31) * mm});
            skLineSegment(sketch, "E563.MirrorCS", {"start": v(293.54, 49.35) * mm, "end": v(293.55, 48.58) * mm});
            skLineSegment(sketch, "E564.MirrorCS", {"start": v(94.22, 46.19) * mm, "end": v(94.21, 46.95) * mm});
            skLineSegment(sketch, "E565.MirrorCS", {"start": v(412.46, 41.74) * mm, "end": v(412.46, 42.5) * mm});
            skLineSegment(sketch, "E566.MirrorCS", {"start": v(520.83, 52.84) * mm, "end": v(520.84, 52.08) * mm});
            skLineSegment(sketch, "E567.MirrorCS", {"start": v(287.2, 48.5) * mm, "end": v(287.2, 49.27) * mm});
            skLineSegment(sketch, "E568.MirrorCS", {"start": v(546.43, 52.39) * mm, "end": v(546.43, 51.63) * mm});
            skLineSegment(sketch, "E569.MirrorCS", {"start": v(606.8, 53.88) * mm, "end": v(606.8, 53.12) * mm});
            skLineSegment(sketch, "E570.MirrorCS", {"start": v(613.18, 43.2) * mm, "end": v(613.18, 43.95) * mm});
            skLineSegment(sketch, "E571.MirrorCS", {"start": v(540.09, 51.55) * mm, "end": v(540.08, 52.31) * mm});
            skLineSegment(sketch, "E572.MirrorCS", {"start": v(184.49, 48.03) * mm, "end": v(184.48, 48.8) * mm});
            skLineSegment(sketch, "E573.MirrorCS", {"start": v(54.82, 46.47) * mm, "end": v(54.83, 45.71) * mm});
            skLineSegment(sketch, "E574.MirrorCS", {"start": v(184.5, 32.16) * mm, "end": v(184.5, 32.92) * mm});
            skLineSegment(sketch, "E575.MirrorCS", {"start": v(478.9, 41.46) * mm, "end": v(478.9, 42.22) * mm});
            skLineSegment(sketch, "E576.MirrorCS", {"start": v(178.13, 48.72) * mm, "end": v(178.14, 47.96) * mm});
            skLineSegment(sketch, "E577.MirrorCS", {"start": v(259.27, 48.93) * mm, "end": v(259.28, 48.17) * mm});
            skLineSegment(sketch, "E578.MirrorCS", {"start": v(48.48, 45.64) * mm, "end": v(48.47, 46.4) * mm});
            skLineSegment(sketch, "E579.MirrorCS", {"start": v(178.15, 32.9) * mm, "end": v(178.15, 32.15) * mm});
            skLineSegment(sketch, "E580.MirrorCS", {"start": v(48.46, 39.88) * mm, "end": v(48.47, 39.12) * mm});
            skLineSegment(sketch, "E581.MirrorCS", {"start": v(478.87, 52.34) * mm, "end": v(478.88, 51.58) * mm});
            skLineSegment(sketch, "E582.MirrorCS", {"start": v(606.82, 52.35) * mm, "end": v(606.8, 53.12) * mm});
            skLineSegment(sketch, "E583.MirrorCS", {"start": v(520.85, 51.32) * mm, "end": v(520.84, 52.08) * mm});
            skLineSegment(sketch, "E584.MirrorCS", {"start": v(6.35, 45.9) * mm, "end": v(6.36, 45.13) * mm});
            skLineSegment(sketch, "E585.MirrorCS", {"start": v(356.42, 50.1) * mm, "end": v(356.42, 50.86) * mm});
            skLineSegment(sketch, "E586.MirrorCS", {"start": v(54.82, 46.47) * mm, "end": v(54.8, 47.24) * mm});
            skLineSegment(sketch, "E587.MirrorCS", {"start": v(325.9, 41.12) * mm, "end": v(325.91, 40.36) * mm});
            skLineSegment(sketch, "E588.MirrorCS", {"start": v(137.4, 39) * mm, "end": v(137.4, 39.76) * mm});
            skLineSegment(sketch, "E589.MirrorCS", {"start": v(293.56, 40.89) * mm, "end": v(293.55, 41.65) * mm});
            skLineSegment(sketch, "E590.MirrorCS", {"start": v(6.35, 45.9) * mm, "end": v(6.34, 46.65) * mm});
            skLineSegment(sketch, "E591.MirrorCS", {"start": v(6.35, 52.97) * mm, "end": v(6.36, 52.2) * mm});
            skLineSegment(sketch, "E592.MirrorCS", {"start": v(48.48, 52.92) * mm, "end": v(48.46, 53.68) * mm});
            skLineSegment(sketch, "E593.MirrorCS", {"start": v(54.81, 53.79) * mm, "end": v(54.83, 53.03) * mm});
            skLineSegment(sketch, "E594.MirrorCS", {"start": v(94.22, 53.69) * mm, "end": v(94.2, 54.45) * mm});
            skLineSegment(sketch, "E595.MirrorCS", {"start": v(100.56, 54.56) * mm, "end": v(100.57, 53.8) * mm});
            skLineSegment(sketch, "E596.MirrorCS", {"start": v(350.07, 50.79) * mm, "end": v(350.07, 50.03) * mm});
            skLineSegment(sketch, "E597.MirrorCS", {"start": v(100.57, 39.5) * mm, "end": v(100.57, 38.73) * mm});
            skLineSegment(sketch, "E598.MirrorCS", {"start": v(178.15, 31.38) * mm, "end": v(178.15, 32.15) * mm});
            skLineSegment(sketch, "E599.MirrorCS", {"start": v(259.27, 48.93) * mm, "end": v(259.26, 49.7) * mm});
            skLineSegment(sketch, "E600.MirrorCS", {"start": v(378.9, 49.61) * mm, "end": v(378.9, 50.37) * mm});
            skLineSegment(sketch, "E601.MirrorCS", {"start": v(259.29, 40.64) * mm, "end": v(259.3, 39.88) * mm});
            skLineSegment(sketch, "E602.MirrorCS", {"start": v(412.46, 41.74) * mm, "end": v(412.47, 40.98) * mm});
            skLineSegment(sketch, "E603.MirrorCS", {"start": v(48.47, 38.35) * mm, "end": v(48.47, 39.12) * mm});
            skLineSegment(sketch, "E604.MirrorCS", {"start": v(478.88, 50.81) * mm, "end": v(478.88, 51.58) * mm});
            skLineSegment(sketch, "E605.MirrorCS", {"start": v(48.46, 47.16) * mm, "end": v(48.47, 46.4) * mm});
            skLineSegment(sketch, "E606.MirrorCS", {"start": v(222.98, 40.38) * mm, "end": v(222.97, 41.14) * mm});
            skLineSegment(sketch, "E607.MirrorCS", {"start": v(293.56, 40.89) * mm, "end": v(293.56, 40.12) * mm});
            skLineSegment(sketch, "E608.MirrorCS", {"start": v(325.9, 49.74) * mm, "end": v(325.88, 50.5) * mm});
            skLineSegment(sketch, "E609.MirrorCS", {"start": v(606.83, 43.9) * mm, "end": v(606.83, 43.15) * mm});
            skLineSegment(sketch, "E610.MirrorCS", {"start": v(184.49, 48.03) * mm, "end": v(184.5, 47.27) * mm});
            skLineSegment(sketch, "E611.MirrorCS", {"start": v(378.88, 51.14) * mm, "end": v(378.9, 50.37) * mm});
            skLineSegment(sketch, "E612.MirrorCS", {"start": v(94.2, 47.71) * mm, "end": v(94.21, 46.95) * mm});
            skLineSegment(sketch, "E613.MirrorCS", {"start": v(6.35, 38.81) * mm, "end": v(6.34, 39.57) * mm});
            skLineSegment(sketch, "E614.MirrorCS", {"start": v(6.35, 52.97) * mm, "end": v(6.34, 53.73) * mm});
            skLineSegment(sketch, "E615.MirrorCS", {"start": v(293.54, 49.35) * mm, "end": v(293.54, 50.1) * mm});
            skLineSegment(sketch, "E616.MirrorCS", {"start": v(54.82, 39.16) * mm, "end": v(54.81, 39.92) * mm});
            skLineSegment(sketch, "E617.MirrorCS", {"start": v(613.18, 43.2) * mm, "end": v(613.19, 42.43) * mm});
            skLineSegment(sketch, "E618.MirrorCS", {"start": v(287.19, 50.03) * mm, "end": v(287.2, 49.27) * mm});
            skLineSegment(sketch, "E619.MirrorCS", {"start": v(319.55, 48.9) * mm, "end": v(319.54, 49.66) * mm});
            skLineSegment(sketch, "E620.MirrorCS", {"start": v(478.9, 42.99) * mm, "end": v(478.9, 42.22) * mm});
            skLineSegment(sketch, "E621.MirrorCS", {"start": v(100.57, 39.5) * mm, "end": v(100.56, 40.25) * mm});
            skLineSegment(sketch, "E622.MirrorCS", {"start": v(222.98, 40.38) * mm, "end": v(222.98, 39.61) * mm});
            skLineSegment(sketch, "E623.MirrorCS", {"start": v(606.84, 42.38) * mm, "end": v(606.83, 43.15) * mm});
            skLineSegment(sketch, "E624.MirrorCS", {"start": v(259.29, 40.64) * mm, "end": v(259.28, 41.4) * mm});
            skLineSegment(sketch, "E625.MirrorCS", {"start": v(137.4, 40.52) * mm, "end": v(137.4, 39.76) * mm});
            skLineSegment(sketch, "E626.MirrorCS", {"start": v(581.68, 62.66) * mm, "end": v(581.66, 63.42) * mm});
            skLineSegment(sketch, "E627.MirrorCS", {"start": v(216.61, 55.75) * mm, "end": v(216.6, 56.51) * mm});
            skLineSegment(sketch, "E628.MirrorCS", {"start": v(94.22, 31.18) * mm, "end": v(94.22, 31.94) * mm});
            skLineSegment(sketch, "E629.MirrorCS", {"start": v(143.75, 39.8) * mm, "end": v(143.74, 40.57) * mm});
            skLineSegment(sketch, "E630.MirrorCS", {"start": v(575.39, 43.68) * mm, "end": v(575.4, 42.92) * mm});
            skLineSegment(sketch, "E631.MirrorCS", {"start": v(500.46, 52.6) * mm, "end": v(500.46, 51.84) * mm});
            skLineSegment(sketch, "E632.MirrorCS", {"start": v(438.12, 51.09) * mm, "end": v(438.13, 50.32) * mm});
            skLineSegment(sketch, "E633.MirrorCS", {"start": v(546.43, 52.39) * mm, "end": v(546.42, 53.15) * mm});
            skLineSegment(sketch, "E634.MirrorCS", {"start": v(462.35, 51.38) * mm, "end": v(462.34, 52.14) * mm});
            skLineSegment(sketch, "E635.MirrorCS", {"start": v(431.78, 50.25) * mm, "end": v(431.77, 51) * mm});
            skLineSegment(sketch, "E636.MirrorCS", {"start": v(575.31, 63.32) * mm, "end": v(575.33, 62.55) * mm});
            skLineSegment(sketch, "E637.MirrorCS", {"start": v(178.15, 39.3) * mm, "end": v(178.15, 40.05) * mm});
            skLineSegment(sketch, "E638.MirrorCS", {"start": v(431.76, 51.77) * mm, "end": v(431.77, 51) * mm});
            skLineSegment(sketch, "E639.MirrorCS", {"start": v(54.82, 31.85) * mm, "end": v(54.82, 31.09) * mm});
            skLineSegment(sketch, "E640.MirrorCS", {"start": v(485.23, 51.65) * mm, "end": v(485.22, 52.41) * mm});
            skLineSegment(sketch, "E641.MirrorCS", {"start": v(438.12, 51.09) * mm, "end": v(438.1, 51.85) * mm});
            skLineSegment(sketch, "E642.MirrorCS", {"start": v(412.44, 50.78) * mm, "end": v(412.45, 50.01) * mm});
            skLineSegment(sketch, "E643.MirrorCS", {"start": v(48.47, 31.07) * mm, "end": v(48.47, 31.83) * mm});
            skLineSegment(sketch, "E644.MirrorCS", {"start": v(456.02, 42.82) * mm, "end": v(456.02, 42.06) * mm});
            skLineSegment(sketch, "E645.MirrorCS", {"start": v(137.4, 32.81) * mm, "end": v(137.4, 32.05) * mm});
            skLineSegment(sketch, "E646.MirrorCS", {"start": v(385.22, 59.35) * mm, "end": v(385.2, 60.11) * mm});
            skLineSegment(sketch, "E647.MirrorCS", {"start": v(293.52, 57.8) * mm, "end": v(293.51, 58.57) * mm});
            skLineSegment(sketch, "E648.MirrorCS", {"start": v(385.24, 50.45) * mm, "end": v(385.25, 49.69) * mm});
            skLineSegment(sketch, "E649.MirrorCS", {"start": v(100.56, 47.03) * mm, "end": v(100.55, 47.79) * mm});
            skLineSegment(sketch, "E650.MirrorCS", {"start": v(456.03, 41.3) * mm, "end": v(456.02, 42.06) * mm});
            skLineSegment(sketch, "E651.MirrorCS", {"start": v(564.6, 42.84) * mm, "end": v(564.6, 43.6) * mm});
            skLineSegment(sketch, "E652.MirrorCS", {"start": v(100.57, 31.96) * mm, "end": v(100.57, 32.72) * mm});
            skLineSegment(sketch, "E653.MirrorCS", {"start": v(613.16, 53.2) * mm, "end": v(613.16, 52.43) * mm});
            skLineSegment(sketch, "E654.MirrorCS", {"start": v(252.93, 41.35) * mm, "end": v(252.94, 40.6) * mm});
            skLineSegment(sketch, "E655.MirrorCS", {"start": v(6.35, 31.73) * mm, "end": v(6.35, 30.97) * mm});
            skLineSegment(sketch, "E656.MirrorCS", {"start": v(54.82, 31.85) * mm, "end": v(54.82, 32.61) * mm});
            skLineSegment(sketch, "E657.MirrorCS", {"start": v(527.2, 52.16) * mm, "end": v(527.2, 51.4) * mm});
            skLineSegment(sketch, "E658.MirrorCS", {"start": v(143.75, 39.8) * mm, "end": v(143.75, 39.04) * mm});
            skLineSegment(sketch, "E659.MirrorCS", {"start": v(613.18, 43.95) * mm, "end": v(621.24, 44.01) * mm});
            skLineSegment(sketch, "E660.MirrorCS", {"start": v(94.21, 40.2) * mm, "end": v(94.22, 39.45) * mm});
            skLineSegment(sketch, "E661.MirrorCS", {"start": v(6.35, 31.73) * mm, "end": v(6.35, 32.5) * mm});
            skLineSegment(sketch, "E662.MirrorCS", {"start": v(184.48, 55.97) * mm, "end": v(184.49, 55.2) * mm});
            skLineSegment(sketch, "E663.MirrorCS", {"start": v(54.82, 39.16) * mm, "end": v(54.82, 38.4) * mm});
            skLineSegment(sketch, "E664.MirrorCS", {"start": v(485.23, 51.65) * mm, "end": v(485.23, 50.9) * mm});
            skLineSegment(sketch, "E665.MirrorCS", {"start": v(613.16, 53.2) * mm, "end": v(613.15, 53.95) * mm});
            skLineSegment(sketch, "E666.MirrorCS", {"start": v(178.15, 47.2) * mm, "end": v(178.14, 47.96) * mm});
            skLineSegment(sketch, "E667.MirrorCS", {"start": v(606.75, 63.85) * mm, "end": v(606.76, 63.08) * mm});
            skLineSegment(sketch, "E668.MirrorCS", {"start": v(520.8, 62.4) * mm, "end": v(520.8, 61.64) * mm});
            skLineSegment(sketch, "E669.MirrorCS", {"start": v(527.22, 42.57) * mm, "end": v(527.21, 43.33) * mm});
            skLineSegment(sketch, "E670.MirrorCS", {"start": v(184.48, 55.97) * mm, "end": v(184.46, 56.73) * mm});
            skLineSegment(sketch, "E671.MirrorCS", {"start": v(216.59, 57.27) * mm, "end": v(216.6, 56.51) * mm});
            skLineSegment(sketch, "E672.MirrorCS", {"start": v(178.14, 40.81) * mm, "end": v(178.15, 40.05) * mm});
            skLineSegment(sketch, "E673.MirrorCS", {"start": v(438.14, 41.93) * mm, "end": v(438.13, 42.7) * mm});
            skLineSegment(sketch, "E674.MirrorCS", {"start": v(564.54, 62.37) * mm, "end": v(564.55, 61.61) * mm});
            skLineSegment(sketch, "E675.MirrorCS", {"start": v(621.25, 42.49) * mm, "end": v(621.24, 43.25) * mm});
            skLineSegment(sketch, "E676.MirrorCS", {"start": v(527.2, 52.16) * mm, "end": v(527.18, 52.92) * mm});
            skLineSegment(sketch, "E677.MirrorCS", {"start": v(581.72, 52.81) * mm, "end": v(581.73, 52.05) * mm});
            skLineSegment(sketch, "E678.MirrorCS", {"start": v(143.75, 32.06) * mm, "end": v(143.75, 32.83) * mm});
            skLineSegment(sketch, "E679.MirrorCS", {"start": v(94.22, 38.68) * mm, "end": v(94.22, 39.45) * mm});
            skLineSegment(sketch, "E680.MirrorCS", {"start": v(143.74, 47.54) * mm, "end": v(143.73, 48.3) * mm});
            skLineSegment(sketch, "E681.MirrorCS", {"start": v(575.36, 53.5) * mm, "end": v(575.37, 52.74) * mm});
            skLineSegment(sketch, "E682.MirrorCS", {"start": v(500.47, 51.07) * mm, "end": v(500.46, 51.84) * mm});
            skLineSegment(sketch, "E683.MirrorCS", {"start": v(184.5, 32.16) * mm, "end": v(184.5, 31.4) * mm});
            skLineSegment(sketch, "E684.MirrorCS", {"start": v(520.86, 43.29) * mm, "end": v(520.87, 42.53) * mm});
            skLineSegment(sketch, "E685.MirrorCS", {"start": v(412.44, 50.78) * mm, "end": v(412.43, 51.54) * mm});
            skLineSegment(sketch, "E686.MirrorCS", {"start": v(293.52, 57.8) * mm, "end": v(293.54, 57.05) * mm});
            skLineSegment(sketch, "E687.MirrorCS", {"start": v(438.09, 60.24) * mm, "end": v(438.1, 59.48) * mm});
            skLineSegment(sketch, "E688.MirrorCS", {"start": v(252.94, 39.83) * mm, "end": v(252.94, 40.6) * mm});
            skLineSegment(sketch, "E689.MirrorCS", {"start": v(406.12, 40.94) * mm, "end": v(406.11, 41.7) * mm});
            skLineSegment(sketch, "E690.MirrorCS", {"start": v(527.22, 42.57) * mm, "end": v(527.22, 41.81) * mm});
            skLineSegment(sketch, "E691.MirrorCS", {"start": v(613.19, 42.43) * mm, "end": v(621.25, 42.49) * mm});
            skLineSegment(sketch, "E692.MirrorCS", {"start": v(575.38, 51.97) * mm, "end": v(575.37, 52.74) * mm});
            skLineSegment(sketch, "E693.MirrorCS", {"start": v(438.09, 60.24) * mm, "end": v(438.08, 61) * mm});
            skLineSegment(sketch, "E694.MirrorCS", {"start": v(178.11, 56.63) * mm, "end": v(178.13, 55.86) * mm});
            skLineSegment(sketch, "E695.MirrorCS", {"start": v(143.74, 47.54) * mm, "end": v(143.75, 46.78) * mm});
            skLineSegment(sketch, "E696.MirrorCS", {"start": v(94.22, 32.7) * mm, "end": v(94.22, 31.94) * mm});
            skLineSegment(sketch, "E697.MirrorCS", {"start": v(143.75, 32.06) * mm, "end": v(143.75, 31.3) * mm});
            skLineSegment(sketch, "E698.MirrorCS", {"start": v(385.24, 50.45) * mm, "end": v(385.23, 51.21) * mm});
            skLineSegment(sketch, "E699.MirrorCS", {"start": v(462.35, 51.38) * mm, "end": v(462.36, 50.62) * mm});
            skLineSegment(sketch, "E700.MirrorCS", {"start": v(591.49, 63.59) * mm, "end": v(591.5, 62.83) * mm});
            skLineSegment(sketch, "E701.MirrorCS", {"start": v(137.4, 31.29) * mm, "end": v(137.4, 32.05) * mm});
            skLineSegment(sketch, "E702.MirrorCS", {"start": v(406.1, 42.46) * mm, "end": v(406.11, 41.7) * mm});
            skLineSegment(sketch, "E703.MirrorCS", {"start": v(520.87, 41.76) * mm, "end": v(520.87, 42.53) * mm});
            skLineSegment(sketch, "E704.MirrorCS", {"start": v(564.58, 52.6) * mm, "end": v(564.59, 51.85) * mm});
            skLineSegment(sketch, "E705.MirrorCS", {"start": v(520.82, 60.87) * mm, "end": v(520.8, 61.64) * mm});
            skLineSegment(sketch, "E706.MirrorCS", {"start": v(621.24, 44.01) * mm, "end": v(621.24, 43.25) * mm});
            skLineSegment(sketch, "E707.MirrorCS", {"start": v(100.56, 47.03) * mm, "end": v(100.57, 46.26) * mm});
            skLineSegment(sketch, "E708.MirrorCS", {"start": v(385.22, 59.35) * mm, "end": v(385.23, 58.6) * mm});
            skLineSegment(sketch, "E709.MirrorCS", {"start": v(606.78, 62.32) * mm, "end": v(606.76, 63.08) * mm});
            skLineSegment(sketch, "E710.MirrorCS", {"start": v(100.57, 31.96) * mm, "end": v(100.57, 31.2) * mm});
            skLineSegment(sketch, "E711.MirrorCS", {"start": v(558.24, 51.77) * mm, "end": v(558.23, 52.53) * mm});
            skLineSegment(sketch, "E712.MirrorCS", {"start": v(558.22, 53.3) * mm, "end": v(558.23, 52.53) * mm});
            skLineSegment(sketch, "E713.MirrorCS", {"start": v(378.88, 58.48) * mm, "end": v(378.87, 59.25) * mm});
            skLineSegment(sketch, "E714.MirrorCS", {"start": v(506.78, 61.4) * mm, "end": v(506.8, 60.64) * mm});
            skLineSegment(sketch, "E715.MirrorCS", {"start": v(597.86, 62.17) * mm, "end": v(606.78, 62.32) * mm});
            skLineSegment(sketch, "E716.MirrorCS", {"start": v(293.57, 32.42) * mm, "end": v(293.57, 31.66) * mm});
            skLineSegment(sketch, "E717.MirrorCS", {"start": v(500.5, 41.62) * mm, "end": v(500.49, 42.38) * mm});
            skLineSegment(sketch, "E718.MirrorCS", {"start": v(597.92, 43.08) * mm, "end": v(597.92, 42.32) * mm});
            skLineSegment(sketch, "E719.MirrorCS", {"start": v(222.97, 48.5) * mm, "end": v(222.96, 49.26) * mm});
            skLineSegment(sketch, "E720.MirrorCS", {"start": v(259.26, 57.23) * mm, "end": v(259.24, 58) * mm});
            skLineSegment(sketch, "E721.MirrorCS", {"start": v(597.92, 43.08) * mm, "end": v(597.91, 43.84) * mm});
            skLineSegment(sketch, "E722.MirrorCS", {"start": v(356.44, 41.34) * mm, "end": v(356.45, 40.58) * mm});
            skLineSegment(sketch, "E723.MirrorCS", {"start": v(143.73, 55.28) * mm, "end": v(143.72, 56.05) * mm});
            skLineSegment(sketch, "E724.MirrorCS", {"start": v(500.44, 60.53) * mm, "end": v(500.43, 61.3) * mm});
            skLineSegment(sketch, "E725.MirrorCS", {"start": v(597.85, 62.93) * mm, "end": v(597.86, 62.17) * mm});
            skLineSegment(sketch, "E726.MirrorCS", {"start": v(325.87, 58.35) * mm, "end": v(325.86, 59.11) * mm});
            skLineSegment(sketch, "E727.MirrorCS", {"start": v(597.91, 43.84) * mm, "end": v(606.83, 43.9) * mm});
            skLineSegment(sketch, "E728.MirrorCS", {"start": v(350.09, 42.06) * mm, "end": v(350.1, 41.3) * mm});
            skLineSegment(sketch, "E729.MirrorCS", {"start": v(485.25, 42.27) * mm, "end": v(485.25, 41.5) * mm});
            skLineSegment(sketch, "E730.MirrorCS", {"start": v(581.7, 53.58) * mm, "end": v(591.53, 53.7) * mm});
            skLineSegment(sketch, "E731.MirrorCS", {"start": v(591.51, 62.06) * mm, "end": v(591.5, 62.83) * mm});
            skLineSegment(sketch, "E732.MirrorCS", {"start": v(597.85, 62.93) * mm, "end": v(597.84, 63.7) * mm});
            skLineSegment(sketch, "E733.MirrorCS", {"start": v(350.1, 40.53) * mm, "end": v(350.1, 41.3) * mm});
            skLineSegment(sketch, "E734.MirrorCS", {"start": v(581.74, 42.97) * mm, "end": v(581.75, 42.2) * mm});
            skLineSegment(sketch, "E735.MirrorCS", {"start": v(621.23, 52.53) * mm, "end": v(621.22, 53.29) * mm});
            skLineSegment(sketch, "E736.MirrorCS", {"start": v(597.84, 63.7) * mm, "end": v(606.75, 63.85) * mm});
            skLineSegment(sketch, "E737.MirrorCS", {"start": v(485.2, 61.04) * mm, "end": v(485.2, 60.27) * mm});
            skLineSegment(sketch, "E738.MirrorCS", {"start": v(581.69, 61.9) * mm, "end": v(591.51, 62.06) * mm});
            skLineSegment(sketch, "E739.MirrorCS", {"start": v(613.11, 63.2) * mm, "end": v(613.1, 63.95) * mm});
            skLineSegment(sketch, "E740.MirrorCS", {"start": v(506.84, 42.42) * mm, "end": v(506.83, 43.19) * mm});
            skLineSegment(sketch, "E741.MirrorCS", {"start": v(287.2, 41.6) * mm, "end": v(287.2, 40.84) * mm});
            skLineSegment(sketch, "E742.MirrorCS", {"start": v(558.25, 43.56) * mm, "end": v(558.26, 42.8) * mm});
            skLineSegment(sketch, "E743.MirrorCS", {"start": v(558.26, 42.03) * mm, "end": v(558.26, 42.8) * mm});
            skLineSegment(sketch, "E744.MirrorCS", {"start": v(216.63, 31.48) * mm, "end": v(216.63, 32.24) * mm});
            skLineSegment(sketch, "E745.MirrorCS", {"start": v(564.55, 61.61) * mm, "end": v(575.34, 61.8) * mm});
            skLineSegment(sketch, "E746.MirrorCS", {"start": v(325.87, 58.35) * mm, "end": v(325.88, 57.6) * mm});
            skLineSegment(sketch, "E747.MirrorCS", {"start": v(222.97, 48.5) * mm, "end": v(222.97, 47.74) * mm});
            skLineSegment(sketch, "E748.MirrorCS", {"start": v(621.2, 54.05) * mm, "end": v(621.22, 53.29) * mm});
            skLineSegment(sketch, "E749.MirrorCS", {"start": v(319.56, 40.31) * mm, "end": v(319.56, 41.07) * mm});
            skLineSegment(sketch, "E750.MirrorCS", {"start": v(564.6, 43.6) * mm, "end": v(575.39, 43.68) * mm});
            skLineSegment(sketch, "E751.MirrorCS", {"start": v(564.6, 42.84) * mm, "end": v(564.61, 42.08) * mm});
            skLineSegment(sketch, "E752.MirrorCS", {"start": v(575.34, 61.8) * mm, "end": v(575.33, 62.55) * mm});
            skLineSegment(sketch, "E753.MirrorCS", {"start": v(378.85, 60) * mm, "end": v(378.87, 59.25) * mm});
            skLineSegment(sketch, "E754.MirrorCS", {"start": v(406.08, 51.46) * mm, "end": v(406.1, 50.7) * mm});
            skLineSegment(sketch, "E755.MirrorCS", {"start": v(462.37, 42.1) * mm, "end": v(462.38, 41.34) * mm});
            skLineSegment(sketch, "E756.MirrorCS", {"start": v(385.26, 41.55) * mm, "end": v(385.26, 42.3) * mm});
            skLineSegment(sketch, "E757.MirrorCS", {"start": v(564.61, 42.08) * mm, "end": v(575.4, 42.16) * mm});
            skLineSegment(sketch, "E758.MirrorCS", {"start": v(581.68, 62.66) * mm, "end": v(581.69, 61.9) * mm});
            skLineSegment(sketch, "E759.MirrorCS", {"start": v(478.86, 60.17) * mm, "end": v(478.84, 60.93) * mm});
            skLineSegment(sketch, "E760.MirrorCS", {"start": v(527.16, 61.74) * mm, "end": v(527.14, 62.5) * mm});
            skLineSegment(sketch, "E761.MirrorCS", {"start": v(506.78, 61.4) * mm, "end": v(506.77, 62.16) * mm});
            skLineSegment(sketch, "E762.MirrorCS", {"start": v(406.1, 49.94) * mm, "end": v(406.1, 50.7) * mm});
            skLineSegment(sketch, "E763.MirrorCS", {"start": v(252.93, 48.1) * mm, "end": v(252.92, 48.86) * mm});
            skLineSegment(sketch, "E764.MirrorCS", {"start": v(591.53, 53.7) * mm, "end": v(591.54, 52.93) * mm});
            skLineSegment(sketch, "E765.MirrorCS", {"start": v(613.16, 52.43) * mm, "end": v(621.23, 52.53) * mm});
            skLineSegment(sketch, "E766.MirrorCS", {"start": v(378.9, 42.26) * mm, "end": v(378.91, 41.5) * mm});
            skLineSegment(sketch, "E767.MirrorCS", {"start": v(575.4, 42.16) * mm, "end": v(575.4, 42.92) * mm});
            skLineSegment(sketch, "E768.MirrorCS", {"start": v(178.14, 55.1) * mm, "end": v(178.13, 55.86) * mm});
            skLineSegment(sketch, "E769.MirrorCS", {"start": v(143.73, 55.28) * mm, "end": v(143.74, 54.52) * mm});
            skLineSegment(sketch, "E770.MirrorCS", {"start": v(431.78, 42.65) * mm, "end": v(431.79, 41.88) * mm});
            skLineSegment(sketch, "E771.MirrorCS", {"start": v(540.1, 41.9) * mm, "end": v(540.1, 42.67) * mm});
            skLineSegment(sketch, "E772.MirrorCS", {"start": v(597.88, 53.77) * mm, "end": v(606.8, 53.88) * mm});
            skLineSegment(sketch, "E773.MirrorCS", {"start": v(431.73, 60.9) * mm, "end": v(431.74, 60.14) * mm});
            skLineSegment(sketch, "E774.MirrorCS", {"start": v(581.73, 52.05) * mm, "end": v(591.55, 52.17) * mm});
            skLineSegment(sketch, "E775.MirrorCS", {"start": v(546.39, 62.07) * mm, "end": v(546.37, 62.83) * mm});
            skLineSegment(sketch, "E776.MirrorCS", {"start": v(546.39, 62.07) * mm, "end": v(546.4, 61.3) * mm});
            skLineSegment(sketch, "E777.MirrorCS", {"start": v(581.66, 63.42) * mm, "end": v(591.49, 63.59) * mm});
            skLineSegment(sketch, "E778.MirrorCS", {"start": v(597.9, 52.25) * mm, "end": v(606.82, 52.35) * mm});
            skLineSegment(sketch, "E779.MirrorCS", {"start": v(581.72, 52.81) * mm, "end": v(581.7, 53.58) * mm});
            skLineSegment(sketch, "E780.MirrorCS", {"start": v(137.38, 48.23) * mm, "end": v(137.4, 47.47) * mm});
            skLineSegment(sketch, "E781.MirrorCS", {"start": v(506.81, 51.91) * mm, "end": v(506.82, 51.15) * mm});
            skLineSegment(sketch, "E782.MirrorCS", {"start": v(485.25, 42.27) * mm, "end": v(485.24, 43.03) * mm});
            skLineSegment(sketch, "E783.MirrorCS", {"start": v(564.54, 62.37) * mm, "end": v(564.53, 63.13) * mm});
            skLineSegment(sketch, "E784.MirrorCS", {"start": v(564.53, 63.13) * mm, "end": v(575.31, 63.32) * mm});
            skLineSegment(sketch, "E785.MirrorCS", {"start": v(319.53, 57.48) * mm, "end": v(319.52, 58.25) * mm});
            skLineSegment(sketch, "E786.MirrorCS", {"start": v(455.98, 59.78) * mm, "end": v(455.97, 60.54) * mm});
            skLineSegment(sketch, "E787.MirrorCS", {"start": v(506.81, 51.91) * mm, "end": v(506.8, 52.67) * mm});
            skLineSegment(sketch, "E788.MirrorCS", {"start": v(540.1, 43.43) * mm, "end": v(540.1, 42.67) * mm});
            skLineSegment(sketch, "E789.MirrorCS", {"start": v(319.55, 41.84) * mm, "end": v(319.56, 41.07) * mm});
            skLineSegment(sketch, "E790.MirrorCS", {"start": v(500.48, 43.14) * mm, "end": v(500.49, 42.38) * mm});
            skLineSegment(sketch, "E791.MirrorCS", {"start": v(438.14, 41.93) * mm, "end": v(438.14, 41.17) * mm});
            skLineSegment(sketch, "E792.MirrorCS", {"start": v(597.9, 53) * mm, "end": v(597.9, 52.25) * mm});
            skLineSegment(sketch, "E793.MirrorCS", {"start": v(558.18, 63.03) * mm, "end": v(558.2, 62.27) * mm});
            skLineSegment(sketch, "E794.MirrorCS", {"start": v(455.96, 61.3) * mm, "end": v(455.97, 60.54) * mm});
            skLineSegment(sketch, "E795.MirrorCS", {"start": v(558.2, 61.5) * mm, "end": v(558.2, 62.27) * mm});
            skLineSegment(sketch, "E796.MirrorCS", {"start": v(462.37, 42.1) * mm, "end": v(462.37, 42.87) * mm});
            skLineSegment(sketch, "E797.MirrorCS", {"start": v(546.45, 42.71) * mm, "end": v(546.46, 41.95) * mm});
            skLineSegment(sketch, "E798.MirrorCS", {"start": v(546.45, 42.71) * mm, "end": v(546.45, 43.47) * mm});
            skLineSegment(sketch, "E799.MirrorCS", {"start": v(287.21, 40.08) * mm, "end": v(287.2, 40.84) * mm});
            skLineSegment(sketch, "E800.MirrorCS", {"start": v(431.8, 41.12) * mm, "end": v(431.79, 41.88) * mm});
            skLineSegment(sketch, "E801.MirrorCS", {"start": v(591.55, 52.17) * mm, "end": v(591.54, 52.93) * mm});
            skLineSegment(sketch, "E802.MirrorCS", {"start": v(597.9, 53) * mm, "end": v(597.88, 53.77) * mm});
            skLineSegment(sketch, "E803.MirrorCS", {"start": v(319.5, 59) * mm, "end": v(319.52, 58.25) * mm});
            skLineSegment(sketch, "E804.MirrorCS", {"start": v(500.42, 62.05) * mm, "end": v(500.43, 61.3) * mm});
            skLineSegment(sketch, "E805.MirrorCS", {"start": v(506.84, 42.42) * mm, "end": v(506.84, 41.66) * mm});
            skLineSegment(sketch, "E806.MirrorCS", {"start": v(48.47, 32.6) * mm, "end": v(48.47, 31.83) * mm});
            skLineSegment(sketch, "E807.MirrorCS", {"start": v(597.92, 42.32) * mm, "end": v(606.84, 42.38) * mm});
            skLineSegment(sketch, "E808.MirrorCS", {"start": v(613.15, 53.95) * mm, "end": v(621.2, 54.05) * mm});
            skLineSegment(sketch, "E809.MirrorCS", {"start": v(456, 52.06) * mm, "end": v(456, 51.3) * mm});
            skLineSegment(sketch, "E810.MirrorCS", {"start": v(485.2, 61.04) * mm, "end": v(485.18, 61.8) * mm});
            skLineSegment(sketch, "E811.MirrorCS", {"start": v(259.26, 57.23) * mm, "end": v(259.27, 56.47) * mm});
            skLineSegment(sketch, "E812.MirrorCS", {"start": v(591.56, 43.8) * mm, "end": v(591.57, 43.04) * mm});
            skLineSegment(sketch, "E813.MirrorCS", {"start": v(252.91, 49.62) * mm, "end": v(252.92, 48.86) * mm});
            skLineSegment(sketch, "E814.MirrorCS", {"start": v(564.59, 51.85) * mm, "end": v(575.38, 51.97) * mm});
            skLineSegment(sketch, "E815.MirrorCS", {"start": v(137.4, 46.7) * mm, "end": v(137.4, 47.47) * mm});
            skLineSegment(sketch, "E816.MirrorCS", {"start": v(527.16, 61.74) * mm, "end": v(527.17, 60.98) * mm});
            skLineSegment(sketch, "E817.MirrorCS", {"start": v(293.57, 32.42) * mm, "end": v(293.56, 33.19) * mm});
            skLineSegment(sketch, "E818.MirrorCS", {"start": v(356.44, 41.34) * mm, "end": v(356.44, 42.1) * mm});
            skLineSegment(sketch, "E819.MirrorCS", {"start": v(456.01, 50.54) * mm, "end": v(456, 51.3) * mm});
            skLineSegment(sketch, "E820.MirrorCS", {"start": v(613.11, 63.2) * mm, "end": v(613.13, 62.43) * mm});
            skLineSegment(sketch, "E821.MirrorCS", {"start": v(216.63, 33) * mm, "end": v(216.63, 32.24) * mm});
            skLineSegment(sketch, "E822.MirrorCS", {"start": v(385.26, 41.55) * mm, "end": v(385.27, 40.79) * mm});
            skLineSegment(sketch, "E823.MirrorCS", {"start": v(564.57, 53.37) * mm, "end": v(575.36, 53.5) * mm});
            skLineSegment(sketch, "E824.MirrorCS", {"start": v(564.58, 52.6) * mm, "end": v(564.57, 53.37) * mm});
            skLineSegment(sketch, "E825.MirrorCS", {"start": v(478.83, 61.7) * mm, "end": v(478.84, 60.93) * mm});
            skLineSegment(sketch, "E826.MirrorCS", {"start": v(581.74, 42.97) * mm, "end": v(581.74, 43.73) * mm});
            skLineSegment(sketch, "E827.MirrorCS", {"start": v(378.92, 40.74) * mm, "end": v(378.91, 41.5) * mm});
            skLineSegment(sketch, "E828.MirrorCS", {"start": v(222.98, 32.25) * mm, "end": v(222.98, 33.02) * mm});
            skLineSegment(sketch, "E829.MirrorCS", {"start": v(137.37, 55.94) * mm, "end": v(137.38, 55.18) * mm});
            skLineSegment(sketch, "E830.MirrorCS", {"start": v(591.57, 42.27) * mm, "end": v(591.57, 43.04) * mm});
            skLineSegment(sketch, "E831.MirrorCS", {"start": v(287.22, 31.65) * mm, "end": v(287.22, 32.4) * mm});
            skLineSegment(sketch, "E832.MirrorCS", {"start": v(581.75, 42.2) * mm, "end": v(591.57, 42.27) * mm});
            skLineSegment(sketch, "E833.MirrorCS", {"start": v(412.41, 59.81) * mm, "end": v(412.4, 60.57) * mm});
            skLineSegment(sketch, "E834.MirrorCS", {"start": v(356.4, 58.87) * mm, "end": v(356.41, 58.1) * mm});
            skLineSegment(sketch, "E835.MirrorCS", {"start": v(350.04, 59.52) * mm, "end": v(350.05, 58.76) * mm});
            skLineSegment(sketch, "E836.MirrorCS", {"start": v(259.3, 32.34) * mm, "end": v(259.3, 31.58) * mm});
            skLineSegment(sketch, "E837.MirrorCS", {"start": v(259.3, 32.34) * mm, "end": v(259.29, 33.1) * mm});
            skLineSegment(sketch, "E838.MirrorCS", {"start": v(462.32, 60.65) * mm, "end": v(462.33, 59.89) * mm});
            skLineSegment(sketch, "E839.MirrorCS", {"start": v(252.9, 57.89) * mm, "end": v(252.9, 57.12) * mm});
            skLineSegment(sketch, "E840.MirrorCS", {"start": v(222.98, 32.25) * mm, "end": v(222.98, 31.5) * mm});
            skLineSegment(sketch, "E841.MirrorCS", {"start": v(613.1, 63.95) * mm, "end": v(621.16, 64.09) * mm});
            skLineSegment(sketch, "E842.MirrorCS", {"start": v(350.06, 58) * mm, "end": v(350.05, 58.76) * mm});
            skLineSegment(sketch, "E843.MirrorCS", {"start": v(252.94, 31.56) * mm, "end": v(252.94, 32.33) * mm});
            skLineSegment(sketch, "E844.MirrorCS", {"start": v(137.4, 54.42) * mm, "end": v(137.38, 55.18) * mm});
            skLineSegment(sketch, "E845.MirrorCS", {"start": v(581.74, 43.73) * mm, "end": v(591.56, 43.8) * mm});
            skLineSegment(sketch, "E846.MirrorCS", {"start": v(462.32, 60.65) * mm, "end": v(462.3, 61.41) * mm});
            skLineSegment(sketch, "E847.MirrorCS", {"start": v(431.75, 59.37) * mm, "end": v(431.74, 60.14) * mm});
            skLineSegment(sketch, "E848.MirrorCS", {"start": v(287.19, 56.94) * mm, "end": v(287.18, 57.7) * mm});
            skLineSegment(sketch, "E849.MirrorCS", {"start": v(540.05, 61.2) * mm, "end": v(540.04, 61.96) * mm});
            skLineSegment(sketch, "E850.MirrorCS", {"start": v(287.16, 58.46) * mm, "end": v(287.18, 57.7) * mm});
            skLineSegment(sketch, "E851.MirrorCS", {"start": v(222.95, 56.62) * mm, "end": v(222.94, 57.38) * mm});
            skLineSegment(sketch, "E852.MirrorCS", {"start": v(540.03, 62.72) * mm, "end": v(540.04, 61.96) * mm});
            skLineSegment(sketch, "E853.MirrorCS", {"start": v(412.41, 59.81) * mm, "end": v(412.43, 59.05) * mm});
            skLineSegment(sketch, "E854.MirrorCS", {"start": v(621.19, 62.56) * mm, "end": v(621.17, 63.33) * mm});
            skLineSegment(sketch, "E855.MirrorCS", {"start": v(406.08, 58.94) * mm, "end": v(406.07, 59.7) * mm});
            skLineSegment(sketch, "E856.MirrorCS", {"start": v(613.13, 62.43) * mm, "end": v(621.19, 62.56) * mm});
            skLineSegment(sketch, "E857.MirrorCS", {"start": v(252.92, 56.36) * mm, "end": v(252.9, 57.12) * mm});
            skLineSegment(sketch, "E858.MirrorCS", {"start": v(252.94, 33.09) * mm, "end": v(252.94, 32.33) * mm});
            skLineSegment(sketch, "E859.MirrorCS", {"start": v(356.4, 58.87) * mm, "end": v(356.39, 59.63) * mm});
            skLineSegment(sketch, "E860.MirrorCS", {"start": v(406.05, 60.47) * mm, "end": v(406.07, 59.7) * mm});
            skLineSegment(sketch, "E861.MirrorCS", {"start": v(621.16, 64.09) * mm, "end": v(621.17, 63.33) * mm});
            skLineSegment(sketch, "E862.MirrorCS", {"start": v(222.95, 56.62) * mm, "end": v(222.96, 55.86) * mm});
            skLineSegment(sketch, "E863.MirrorCS", {"start": v(287.21, 33.17) * mm, "end": v(287.22, 32.4) * mm});
            skLineSegment(sketch, "E864.MirrorCS", {"start": v(406.12, 33.46) * mm, "end": v(406.12, 32.7) * mm});
            skLineSegment(sketch, "E865.MirrorCS", {"start": v(325.91, 32.5) * mm, "end": v(325.91, 33.26) * mm});
            skLineSegment(sketch, "E866.MirrorCS", {"start": v(184.5, 47.27) * mm, "end": v(216.62, 47.66) * mm, "construction": true});
            skLineSegment(sketch, "E867.MirrorCS", {"start": v(356.45, 32.58) * mm, "end": v(356.45, 31.81) * mm});
            skLineSegment(sketch, "E868.MirrorCS", {"start": v(350.1, 31.8) * mm, "end": v(350.1, 32.56) * mm});
            skLineSegment(sketch, "E869.MirrorCS", {"start": v(385.27, 32.65) * mm, "end": v(385.27, 33.4) * mm});
            skLineSegment(sketch, "E870.MirrorCS", {"start": v(325.91, 32.5) * mm, "end": v(325.92, 31.74) * mm});
            skLineSegment(sketch, "E871.MirrorCS", {"start": v(293.55, 48.58) * mm, "end": v(319.55, 48.9) * mm});
            skLineSegment(sketch, "E872.MirrorCS", {"start": v(319.56, 33.25) * mm, "end": v(319.56, 32.49) * mm});
            skLineSegment(sketch, "E873.MirrorCS", {"start": v(184.5, 39.34) * mm, "end": v(216.63, 39.57) * mm, "construction": true});
            skLineSegment(sketch, "E874.MirrorCS", {"start": v(325.88, 50.5) * mm, "end": v(350.07, 50.79) * mm});
            skLineSegment(sketch, "E875.MirrorCS", {"start": v(6.34, 53.73) * mm, "end": v(48.45, 54.44) * mm});
            skLineSegment(sketch, "E876.MirrorCS", {"start": v(184.48, 48.8) * mm, "end": v(216.6, 49.18) * mm, "construction": true});
            skLineSegment(sketch, "E877.MirrorCS", {"start": v(259.28, 48.17) * mm, "end": v(287.2, 48.5) * mm});
            skLineSegment(sketch, "E878.MirrorCS", {"start": v(54.8, 54.55) * mm, "end": v(94.2, 55.21) * mm});
            skLineSegment(sketch, "E879.MirrorCS", {"start": v(184.5, 32.92) * mm, "end": v(216.63, 33) * mm, "construction": true});
            skLineSegment(sketch, "E880.MirrorCS", {"start": v(356.45, 32.58) * mm, "end": v(356.45, 33.34) * mm});
            skLineSegment(sketch, "E881.MirrorCS", {"start": v(184.49, 55.2) * mm, "end": v(216.61, 55.75) * mm, "construction": true});
            skLineSegment(sketch, "E882.MirrorCS", {"start": v(184.5, 40.86) * mm, "end": v(216.62, 41.1) * mm, "construction": true});
            skLineSegment(sketch, "E883.MirrorCS", {"start": v(350.1, 33.32) * mm, "end": v(350.1, 32.56) * mm});
            skLineSegment(sketch, "E884.MirrorCS", {"start": v(184.5, 31.4) * mm, "end": v(216.63, 31.48) * mm, "construction": true});
            skLineSegment(sketch, "E885.MirrorCS", {"start": v(356.43, 49.34) * mm, "end": v(378.9, 49.61) * mm});
            skLineSegment(sketch, "E886.MirrorCS", {"start": v(412.47, 32.71) * mm, "end": v(412.47, 33.47) * mm});
            skLineSegment(sketch, "E887.MirrorCS", {"start": v(378.92, 33.4) * mm, "end": v(378.92, 32.63) * mm});
            skLineSegment(sketch, "E888.MirrorCS", {"start": v(319.57, 31.73) * mm, "end": v(319.56, 32.49) * mm});
            skLineSegment(sketch, "E889.MirrorCS", {"start": v(293.57, 31.66) * mm, "end": v(319.57, 31.73) * mm});
            skLineSegment(sketch, "E890.MirrorCS", {"start": v(438.13, 50.32) * mm, "end": v(456.01, 50.54) * mm});
            skLineSegment(sketch, "E891.MirrorCS", {"start": v(6.34, 39.57) * mm, "end": v(48.46, 39.88) * mm});
            skLineSegment(sketch, "E892.MirrorCS", {"start": v(356.45, 40.58) * mm, "end": v(378.92, 40.74) * mm});
            skLineSegment(sketch, "E893.MirrorCS", {"start": v(546.43, 51.63) * mm, "end": v(558.24, 51.77) * mm});
            skLineSegment(sketch, "E894.MirrorCS", {"start": v(546.45, 43.47) * mm, "end": v(558.25, 43.56) * mm});
            skLineSegment(sketch, "E895.MirrorCS", {"start": v(54.81, 39.92) * mm, "end": v(94.21, 40.2) * mm});
            skLineSegment(sketch, "E896.MirrorCS", {"start": v(485.25, 41.5) * mm, "end": v(500.5, 41.62) * mm});
            skLineSegment(sketch, "E897.MirrorCS", {"start": v(54.83, 45.71) * mm, "end": v(94.22, 46.19) * mm});
            skLineSegment(sketch, "E898.MirrorCS", {"start": v(356.41, 58.1) * mm, "end": v(378.88, 58.48) * mm});
            skLineSegment(sketch, "E899.MirrorCS", {"start": v(325.91, 33.26) * mm, "end": v(350.1, 33.32) * mm});
            skLineSegment(sketch, "E900.MirrorCS", {"start": v(143.74, 40.57) * mm, "end": v(178.14, 40.81) * mm});
            skLineSegment(sketch, "E901.MirrorCS", {"start": v(184.5, 39.34) * mm, "end": v(216.63, 39.57) * mm});
            skLineSegment(sketch, "E902.MirrorCS", {"start": v(462.34, 52.14) * mm, "end": v(478.87, 52.34) * mm});
            skLineSegment(sketch, "E903.MirrorCS", {"start": v(412.45, 50.01) * mm, "end": v(431.78, 50.25) * mm});
            skLineSegment(sketch, "E904.MirrorCS", {"start": v(546.37, 62.83) * mm, "end": v(558.18, 63.03) * mm});
            skLineSegment(sketch, "E905.MirrorCS", {"start": v(485.2, 60.27) * mm, "end": v(500.44, 60.53) * mm});
            skLineSegment(sketch, "E906.MirrorCS", {"start": v(462.38, 33.6) * mm, "end": v(478.9, 33.63) * mm});
            skLineSegment(sketch, "E907.MirrorCS", {"start": v(259.3, 31.58) * mm, "end": v(287.22, 31.65) * mm});
            skLineSegment(sketch, "E908.MirrorCS", {"start": v(143.75, 39.04) * mm, "end": v(178.15, 39.3) * mm});
            skLineSegment(sketch, "E909.MirrorCS", {"start": v(184.48, 48.8) * mm, "end": v(216.6, 49.18) * mm});
            skLineSegment(sketch, "E910.MirrorCS", {"start": v(527.2, 51.4) * mm, "end": v(540.09, 51.55) * mm});
            skLineSegment(sketch, "E911.MirrorCS", {"start": v(184.49, 55.2) * mm, "end": v(216.61, 55.75) * mm});
            skLineSegment(sketch, "E912.MirrorCS", {"start": v(184.5, 32.92) * mm, "end": v(216.63, 33) * mm});
            skLineSegment(sketch, "E913.MirrorCS", {"start": v(527.21, 43.33) * mm, "end": v(540.1, 43.43) * mm});
            skLineSegment(sketch, "E914.MirrorCS", {"start": v(506.82, 51.15) * mm, "end": v(520.85, 51.32) * mm});
            skLineSegment(sketch, "E915.MirrorCS", {"start": v(259.26, 49.7) * mm, "end": v(287.19, 50.03) * mm});
            skLineSegment(sketch, "E916.MirrorCS", {"start": v(222.97, 41.14) * mm, "end": v(252.93, 41.35) * mm});
            skLineSegment(sketch, "E917.MirrorCS", {"start": v(325.88, 57.6) * mm, "end": v(350.06, 58) * mm});
            skLineSegment(sketch, "E918.MirrorCS", {"start": v(293.51, 58.57) * mm, "end": v(319.5, 59) * mm});
            skLineSegment(sketch, "E919.MirrorCS", {"start": v(385.25, 49.69) * mm, "end": v(406.1, 49.94) * mm});
            skLineSegment(sketch, "E920.MirrorCS", {"start": v(222.97, 47.74) * mm, "end": v(252.93, 48.1) * mm});
            skLineSegment(sketch, "E921.MirrorCS", {"start": v(485.22, 52.41) * mm, "end": v(500.46, 52.6) * mm});
            skLineSegment(sketch, "E922.MirrorCS", {"start": v(385.26, 42.3) * mm, "end": v(406.1, 42.46) * mm});
            skLineSegment(sketch, "E923.MirrorCS", {"start": v(6.36, 45.13) * mm, "end": v(48.48, 45.64) * mm});
            skLineSegment(sketch, "E924.MirrorCS", {"start": v(506.8, 52.67) * mm, "end": v(520.83, 52.84) * mm});
            skLineSegment(sketch, "E925.MirrorCS", {"start": v(462.38, 41.34) * mm, "end": v(478.9, 41.46) * mm});
            skLineSegment(sketch, "E926.MirrorCS", {"start": v(325.91, 40.36) * mm, "end": v(350.1, 40.53) * mm});
            skLineSegment(sketch, "E927.MirrorCS", {"start": v(412.43, 51.54) * mm, "end": v(431.76, 51.77) * mm});
            skLineSegment(sketch, "E928.MirrorCS", {"start": v(293.55, 41.65) * mm, "end": v(319.55, 41.84) * mm});
            skLineSegment(sketch, "E929.MirrorCS", {"start": v(506.85, 33.7) * mm, "end": v(520.88, 33.73) * mm});
            skLineSegment(sketch, "E930.MirrorCS", {"start": v(0, 52.86) * mm, "end": v(646.57, 63.75) * mm, "construction": true});
            skLineSegment(sketch, "E931.MirrorCS", {"start": v(6.36, 52.2) * mm, "end": v(48.48, 52.92) * mm});
            skLineSegment(sketch, "E932.MirrorCS", {"start": v(54.83, 53.03) * mm, "end": v(94.22, 53.69) * mm});
            skLineSegment(sketch, "E933.MirrorCS", {"start": v(143.74, 54.52) * mm, "end": v(178.14, 55.1) * mm});
            skLineSegment(sketch, "E934.MirrorCS", {"start": v(462.37, 42.87) * mm, "end": v(478.9, 42.99) * mm});
            skLineSegment(sketch, "E935.MirrorCS", {"start": v(259.3, 39.88) * mm, "end": v(287.21, 40.08) * mm});
            skLineSegment(sketch, "E936.MirrorCS", {"start": v(412.47, 40.98) * mm, "end": v(431.8, 41.12) * mm});
            skLineSegment(sketch, "E937.MirrorCS", {"start": v(143.73, 48.3) * mm, "end": v(178.13, 48.72) * mm});
            skLineSegment(sketch, "E938.MirrorCS", {"start": v(184.5, 47.27) * mm, "end": v(216.62, 47.66) * mm});
            skLineSegment(sketch, "E939.MirrorCS", {"start": v(325.86, 59.11) * mm, "end": v(350.04, 59.52) * mm});
            skLineSegment(sketch, "E940.MirrorCS", {"start": v(184.46, 56.73) * mm, "end": v(216.59, 57.27) * mm, "construction": true});
            skLineSegment(sketch, "E941.MirrorCS", {"start": v(143.75, 46.78) * mm, "end": v(178.15, 47.2) * mm});
            skLineSegment(sketch, "E942.MirrorCS", {"start": v(438.13, 42.7) * mm, "end": v(456.02, 42.82) * mm});
            skLineSegment(sketch, "E943.MirrorCS", {"start": v(259.27, 56.47) * mm, "end": v(287.19, 56.94) * mm});
            skLineSegment(sketch, "E944.MirrorCS", {"start": v(356.42, 50.86) * mm, "end": v(378.88, 51.14) * mm});
            skLineSegment(sketch, "E945.MirrorCS", {"start": v(293.56, 40.12) * mm, "end": v(319.56, 40.31) * mm});
            skLineSegment(sketch, "E946.MirrorCS", {"start": v(438.14, 41.17) * mm, "end": v(456.03, 41.3) * mm});
            skLineSegment(sketch, "E947.MirrorCS", {"start": v(184.5, 40.86) * mm, "end": v(216.62, 41.1) * mm});
            skLineSegment(sketch, "E948.MirrorCS", {"start": v(222.94, 57.38) * mm, "end": v(252.9, 57.89) * mm});
            skLineSegment(sketch, "E949.MirrorCS", {"start": v(527.22, 41.81) * mm, "end": v(540.1, 41.9) * mm});
            skLineSegment(sketch, "E950.MirrorCS", {"start": v(438.1, 51.85) * mm, "end": v(456, 52.06) * mm});
            skLineSegment(sketch, "E951.MirrorCS", {"start": v(100.56, 40.25) * mm, "end": v(137.4, 40.52) * mm});
            skLineSegment(sketch, "E952.MirrorCS", {"start": v(546.46, 41.95) * mm, "end": v(558.26, 42.03) * mm});
            skLineSegment(sketch, "E953.MirrorCS", {"start": v(6.34, 46.65) * mm, "end": v(48.46, 47.16) * mm});
            skLineSegment(sketch, "E954.MirrorCS", {"start": v(-33.04, 56.39) * mm, "end": v(118.54, 56.39) * mm, "construction": true});
            skLineSegment(sketch, "E955.MirrorCS", {"start": v(527.14, 62.5) * mm, "end": v(540.03, 62.72) * mm});
            skLineSegment(sketch, "E956.MirrorCS", {"start": v(293.54, 57.05) * mm, "end": v(319.53, 57.48) * mm});
            skLineSegment(sketch, "E957.MirrorCS", {"start": v(438.1, 59.48) * mm, "end": v(455.98, 59.78) * mm});
            skLineSegment(sketch, "E958.MirrorCS", {"start": v(54.82, 32.61) * mm, "end": v(94.22, 32.7) * mm});
            skLineSegment(sketch, "E959.MirrorCS", {"start": v(485.26, 32.12) * mm, "end": v(500.5, 32.16) * mm});
            skLineSegment(sketch, "E960.MirrorCS", {"start": v(325.9, 41.88) * mm, "end": v(350.09, 42.06) * mm});
            skLineSegment(sketch, "E961.MirrorCS", {"start": v(54.8, 47.24) * mm, "end": v(94.2, 47.71) * mm});
            skLineSegment(sketch, "E962.MirrorCS", {"start": v(54.82, 38.4) * mm, "end": v(94.22, 38.68) * mm});
            skLineSegment(sketch, "E963.MirrorCS", {"start": v(546.42, 53.15) * mm, "end": v(558.22, 53.3) * mm});
            skLineSegment(sketch, "E964.MirrorCS", {"start": v(485.23, 50.9) * mm, "end": v(500.47, 51.07) * mm});
            skLineSegment(sketch, "E965.MirrorCS", {"start": v(546.4, 61.3) * mm, "end": v(558.2, 61.5) * mm});
            skLineSegment(sketch, "E966.MirrorCS", {"start": v(6.36, 38.05) * mm, "end": v(48.47, 38.35) * mm});
            skLineSegment(sketch, "E967.MirrorCS", {"start": v(293.54, 50.1) * mm, "end": v(319.53, 50.42) * mm});
            skLineSegment(sketch, "E968.MirrorCS", {"start": v(325.9, 48.97) * mm, "end": v(350.08, 49.26) * mm});
            skLineSegment(sketch, "E969.MirrorCS", {"start": v(462.36, 50.62) * mm, "end": v(478.88, 50.81) * mm});
            skLineSegment(sketch, "E970.MirrorCS", {"start": v(527.17, 60.98) * mm, "end": v(540.05, 61.2) * mm});
            skLineSegment(sketch, "E971.MirrorCS", {"start": v(293.56, 33.19) * mm, "end": v(319.56, 33.25) * mm});
            skLineSegment(sketch, "E972.MirrorCS", {"start": v(506.83, 43.19) * mm, "end": v(520.86, 43.29) * mm});
            skLineSegment(sketch, "E973.MirrorCS", {"start": v(412.46, 42.5) * mm, "end": v(431.78, 42.65) * mm});
            skLineSegment(sketch, "E974.MirrorCS", {"start": v(385.23, 51.21) * mm, "end": v(406.08, 51.46) * mm});
            skLineSegment(sketch, "E975.MirrorCS", {"start": v(506.77, 62.16) * mm, "end": v(520.8, 62.4) * mm});
            skLineSegment(sketch, "E976.MirrorCS", {"start": v(385.27, 33.4) * mm, "end": v(406.12, 33.46) * mm});
            skLineSegment(sketch, "E977.MirrorCS", {"start": v(485.24, 43.03) * mm, "end": v(500.48, 43.14) * mm});
            skLineSegment(sketch, "E978.MirrorCS", {"start": v(222.98, 39.61) * mm, "end": v(252.94, 39.83) * mm});
            skLineSegment(sketch, "E979.MirrorCS", {"start": v(385.27, 40.79) * mm, "end": v(406.12, 40.94) * mm});
            skLineSegment(sketch, "E980.MirrorCS", {"start": v(100.57, 46.26) * mm, "end": v(137.4, 46.7) * mm});
            skLineSegment(sketch, "E981.MirrorCS", {"start": v(222.96, 55.86) * mm, "end": v(252.92, 56.36) * mm});
            skLineSegment(sketch, "E982.MirrorCS", {"start": v(527.18, 52.92) * mm, "end": v(540.07, 53.07) * mm});
            skLineSegment(sketch, "E983.MirrorCS", {"start": v(259.28, 41.4) * mm, "end": v(287.2, 41.6) * mm});
            skLineSegment(sketch, "E984.MirrorCS", {"start": v(506.84, 41.66) * mm, "end": v(520.87, 41.76) * mm});
            skLineSegment(sketch, "E985.MirrorCS", {"start": v(222.96, 49.26) * mm, "end": v(252.91, 49.62) * mm});
            skLineSegment(sketch, "E986.MirrorCS", {"start": v(259.24, 58) * mm, "end": v(287.16, 58.46) * mm});
            skLineSegment(sketch, "E987.MirrorCS", {"start": v(506.8, 60.64) * mm, "end": v(520.82, 60.87) * mm});
            skLineSegment(sketch, "E988.MirrorCS", {"start": v(0, 38.77) * mm, "end": v(646.64, 43.43) * mm, "construction": true});
            skLineSegment(sketch, "E989.MirrorCS", {"start": v(356.44, 42.1) * mm, "end": v(378.9, 42.26) * mm});
            skLineSegment(sketch, "E990.MirrorCS", {"start": v(100.57, 32.72) * mm, "end": v(137.4, 32.81) * mm});
            skLineSegment(sketch, "E991.MirrorCS", {"start": v(100.55, 47.79) * mm, "end": v(137.38, 48.23) * mm});
            skLineSegment(sketch, "E992.MirrorCS", {"start": v(356.39, 59.63) * mm, "end": v(378.85, 60) * mm});
            skLineSegment(sketch, "E993.MirrorCS", {"start": v(54.82, 31.09) * mm, "end": v(94.22, 31.18) * mm});
            skLineSegment(sketch, "E994.MirrorCS", {"start": v(462.38, 32.83) * mm, "end": v(462.38, 33.6) * mm});
            skLineSegment(sketch, "E995.MirrorCS", {"start": v(431.8, 33.52) * mm, "end": v(431.8, 32.76) * mm});
            skLineSegment(sketch, "E996.MirrorCS", {"start": v(143.72, 56.05) * mm, "end": v(178.11, 56.63) * mm});
            skLineSegment(sketch, "E997.MirrorCS", {"start": v(438.15, 32.77) * mm, "end": v(438.15, 33.53) * mm});
            skLineSegment(sketch, "E998.MirrorCS", {"start": v(356.45, 33.34) * mm, "end": v(378.92, 33.4) * mm});
            skLineSegment(sketch, "E999.MirrorCS", {"start": v(385.2, 60.11) * mm, "end": v(406.05, 60.47) * mm});
            skLineSegment(sketch, "E1000.MirrorCS", {"start": v(0, 45.05) * mm, "end": v(642.94, 52.79) * mm, "construction": true});
            skLineSegment(sketch, "E1001.MirrorCS", {"start": v(100.57, 38.73) * mm, "end": v(137.4, 39) * mm});
            skLineSegment(sketch, "E1002.MirrorCS", {"start": v(259.29, 33.1) * mm, "end": v(287.21, 33.17) * mm});
            skLineSegment(sketch, "E1003.MirrorCS", {"start": v(478.9, 33.63) * mm, "end": v(478.9, 32.87) * mm});
            skLineSegment(sketch, "E1004.MirrorCS", {"start": v(462.33, 59.89) * mm, "end": v(478.86, 60.17) * mm});
            skLineSegment(sketch, "E1005.MirrorCS", {"start": v(222.98, 31.5) * mm, "end": v(252.94, 31.56) * mm});
            skLineSegment(sketch, "E1006.MirrorCS", {"start": v(485.26, 33.65) * mm, "end": v(500.5, 33.68) * mm});
            skLineSegment(sketch, "E1007.MirrorCS", {"start": v(438.08, 61) * mm, "end": v(455.96, 61.3) * mm});
            skLineSegment(sketch, "E1008.MirrorCS", {"start": v(6.35, 30.97) * mm, "end": v(48.47, 31.07) * mm});
            skLineSegment(sketch, "E1009.MirrorCS", {"start": v(412.47, 33.47) * mm, "end": v(431.8, 33.52) * mm});
            skLineSegment(sketch, "E1010.MirrorCS", {"start": v(0, 52.1) * mm, "end": v(642.9, 62.93) * mm, "construction": true});
            skLineSegment(sketch, "E1011.MirrorCS", {"start": v(100.57, 53.8) * mm, "end": v(137.4, 54.42) * mm});
            skLineSegment(sketch, "E1012.MirrorCS", {"start": v(462.3, 61.41) * mm, "end": v(478.83, 61.7) * mm});
            skLineSegment(sketch, "E1013.MirrorCS", {"start": v(412.43, 59.05) * mm, "end": v(431.75, 59.37) * mm});
            skLineSegment(sketch, "E1014.MirrorCS", {"start": v(143.75, 32.83) * mm, "end": v(178.15, 32.9) * mm});
            skLineSegment(sketch, "E1015.MirrorCS", {"start": v(184.5, 31.4) * mm, "end": v(216.63, 31.48) * mm});
            skLineSegment(sketch, "E1016.MirrorCS", {"start": v(0, 45.82) * mm, "end": v(646.61, 53.6) * mm, "construction": true});
            skLineSegment(sketch, "E1017.MirrorCS", {"start": v(6.35, 32.5) * mm, "end": v(48.47, 32.6) * mm});
            skLineSegment(sketch, "E1018.MirrorCS", {"start": v(546.46, 33.8) * mm, "end": v(558.27, 33.82) * mm});
            skLineSegment(sketch, "E1019.MirrorCS", {"start": v(100.54, 55.32) * mm, "end": v(137.37, 55.94) * mm});
            skLineSegment(sketch, "E1020.MirrorCS", {"start": v(438.15, 33.53) * mm, "end": v(456.03, 33.58) * mm});
            skLineSegment(sketch, "E1021.MirrorCS", {"start": v(143.75, 31.3) * mm, "end": v(178.15, 31.38) * mm});
            skLineSegment(sketch, "E1022.MirrorCS", {"start": v(184.46, 56.73) * mm, "end": v(216.59, 57.27) * mm});
            skLineSegment(sketch, "E1023.MirrorCS", {"start": v(462.39, 32.07) * mm, "end": v(478.91, 32.1) * mm});
            skLineSegment(sketch, "E1024.MirrorCS", {"start": v(412.4, 60.57) * mm, "end": v(431.73, 60.9) * mm});
            skLineSegment(sketch, "E1025.MirrorCS", {"start": v(485.18, 61.8) * mm, "end": v(500.42, 62.05) * mm});
            skLineSegment(sketch, "E1026.MirrorCS", {"start": v(385.23, 58.6) * mm, "end": v(406.08, 58.94) * mm});
            skLineSegment(sketch, "E1027.MirrorCS", {"start": v(222.98, 33.02) * mm, "end": v(252.94, 33.09) * mm});
            skLineSegment(sketch, "E1028.MirrorCS", {"start": v(100.57, 31.2) * mm, "end": v(137.4, 31.29) * mm});
            skLineSegment(sketch, "E1029.MirrorCS", {"start": v(0, 38) * mm, "end": v(642.97, 42.65) * mm, "construction": true});
            skLineSegment(sketch, "E1030.MirrorCS", {"start": v(527.23, 33.75) * mm, "end": v(540.11, 33.78) * mm});
            skLineSegment(sketch, "E1031.MirrorCS", {"start": v(456.03, 33.58) * mm, "end": v(456.03, 32.82) * mm});
            skLineSegment(sketch, "E1032.MirrorCS", {"start": v(325.92, 31.74) * mm, "end": v(350.1, 31.8) * mm});
            skLineSegment(sketch, "E1033.MirrorCS", {"start": v(356.45, 31.81) * mm, "end": v(378.92, 31.87) * mm});
            skLineSegment(sketch, "E1034.MirrorCS", {"start": v(385.27, 32.65) * mm, "end": v(385.27, 31.88) * mm});
            skLineSegment(sketch, "E1035.MirrorCS", {"start": v(385.27, 31.88) * mm, "end": v(406.12, 31.93) * mm});
            skLineSegment(sketch, "E1036.MirrorCS", {"start": v(406.12, 31.93) * mm, "end": v(406.12, 32.7) * mm});
            skLineSegment(sketch, "E1037.MirrorCS", {"start": v(0, 30.96) * mm, "end": v(642.98, 32.5) * mm, "construction": true});
            skLineSegment(sketch, "E1038.MirrorCS", {"start": v(412.47, 31.95) * mm, "end": v(431.8, 32) * mm});
            skLineSegment(sketch, "E1039.MirrorCS", {"start": v(431.8, 32) * mm, "end": v(431.8, 32.76) * mm});
            skLineSegment(sketch, "E1040.MirrorCS", {"start": v(412.47, 32.71) * mm, "end": v(412.47, 31.95) * mm});
            skLineSegment(sketch, "E1041.MirrorCS", {"start": v(438.15, 32.01) * mm, "end": v(456.04, 32.05) * mm});
            skLineSegment(sketch, "E1042.MirrorCS", {"start": v(438.15, 32.77) * mm, "end": v(438.15, 32.01) * mm});
            skLineSegment(sketch, "E1043.MirrorCS", {"start": v(456.04, 32.05) * mm, "end": v(456.03, 32.82) * mm});
            skLineSegment(sketch, "E1044.MirrorCS", {"start": v(506.85, 32.18) * mm, "end": v(520.88, 32.2) * mm});
            skLineSegment(sketch, "E1045.MirrorCS", {"start": v(485.26, 32.89) * mm, "end": v(485.26, 32.12) * mm});
            skLineSegment(sketch, "E1046.MirrorCS", {"start": v(500.5, 32.16) * mm, "end": v(500.5, 32.92) * mm});
            skLineSegment(sketch, "E1047.MirrorCS", {"start": v(500.5, 33.68) * mm, "end": v(500.5, 32.92) * mm});
            skLineSegment(sketch, "E1048.MirrorCS", {"start": v(462.38, 32.83) * mm, "end": v(462.39, 32.07) * mm});
            skLineSegment(sketch, "E1049.MirrorCS", {"start": v(478.91, 32.1) * mm, "end": v(478.9, 32.87) * mm});
            skLineSegment(sketch, "E1050.MirrorCS", {"start": v(485.26, 32.89) * mm, "end": v(485.26, 33.65) * mm});
            skLineSegment(sketch, "E1051.MirrorCS", {"start": v(520.88, 33.73) * mm, "end": v(520.88, 32.97) * mm});
            skLineSegment(sketch, "E1052.MirrorCS", {"start": v(506.85, 32.94) * mm, "end": v(506.85, 33.7) * mm});
            skLineSegment(sketch, "E1053.MirrorCS", {"start": v(0, 31.72) * mm, "end": v(646.66, 33.27) * mm, "construction": true});
            skLineSegment(sketch, "E1054.MirrorCS", {"start": v(506.85, 32.94) * mm, "end": v(506.85, 32.18) * mm});
            skLineSegment(sketch, "E1055.MirrorCS", {"start": v(520.88, 32.2) * mm, "end": v(520.88, 32.97) * mm});
            skLineSegment(sketch, "E1056.MirrorCS", {"start": v(527.23, 32.99) * mm, "end": v(527.23, 32.22) * mm});
            skLineSegment(sketch, "E1057.MirrorCS", {"start": v(527.23, 32.99) * mm, "end": v(527.23, 33.75) * mm});
            skLineSegment(sketch, "E1058.MirrorCS", {"start": v(540.12, 32.26) * mm, "end": v(540.11, 33.02) * mm});
            skLineSegment(sketch, "E1059.MirrorCS", {"start": v(540.11, 33.78) * mm, "end": v(540.11, 33.02) * mm});
            skLineSegment(sketch, "E1060.MirrorCS", {"start": v(527.23, 32.22) * mm, "end": v(540.12, 32.26) * mm});
            skLineSegment(sketch, "E1061.MirrorCS", {"start": v(546.46, 33.03) * mm, "end": v(546.47, 32.27) * mm});
            skLineSegment(sketch, "E1062.MirrorCS", {"start": v(546.47, 32.27) * mm, "end": v(558.27, 32.3) * mm});
            skLineSegment(sketch, "E1063.MirrorCS", {"start": v(558.27, 32.3) * mm, "end": v(558.27, 33.06) * mm});
            skLineSegment(sketch, "E1064.MirrorCS", {"start": v(558.27, 33.82) * mm, "end": v(558.27, 33.06) * mm});
            skLineSegment(sketch, "E1065.MirrorCS", {"start": v(546.46, 33.03) * mm, "end": v(546.46, 33.8) * mm});
            skLineSegment(sketch, "E1066.MirrorCS", {"start": v(621.26, 32.45) * mm, "end": v(621.26, 33.21) * mm});
            skLineSegment(sketch, "E1067.MirrorCS", {"start": v(606.85, 33.94) * mm, "end": v(606.85, 33.18) * mm});
            skLineSegment(sketch, "E1068.MirrorCS", {"start": v(564.62, 33.08) * mm, "end": v(564.62, 33.84) * mm});
            skLineSegment(sketch, "E1069.MirrorCS", {"start": v(564.62, 33.08) * mm, "end": v(564.62, 32.31) * mm});
            skLineSegment(sketch, "E1070.MirrorCS", {"start": v(575.4, 32.34) * mm, "end": v(575.4, 33.1) * mm});
            skLineSegment(sketch, "E1071.MirrorCS", {"start": v(581.76, 33.12) * mm, "end": v(581.76, 32.36) * mm});
            skLineSegment(sketch, "E1072.MirrorCS", {"start": v(613.2, 33.2) * mm, "end": v(613.2, 33.96) * mm});
            skLineSegment(sketch, "E1073.MirrorCS", {"start": v(591.58, 32.38) * mm, "end": v(591.58, 33.14) * mm});
            skLineSegment(sketch, "E1074.MirrorCS", {"start": v(597.93, 33.16) * mm, "end": v(597.93, 33.92) * mm});
            skLineSegment(sketch, "E1075.MirrorCS", {"start": v(597.93, 33.16) * mm, "end": v(597.93, 32.4) * mm});
            skLineSegment(sketch, "E1076.MirrorCS", {"start": v(575.4, 33.86) * mm, "end": v(575.4, 33.1) * mm});
            skLineSegment(sketch, "E1077.MirrorCS", {"start": v(581.76, 33.12) * mm, "end": v(581.75, 33.88) * mm});
            skLineSegment(sketch, "E1078.MirrorCS", {"start": v(606.85, 32.42) * mm, "end": v(606.85, 33.18) * mm});
            skLineSegment(sketch, "E1079.MirrorCS", {"start": v(621.26, 33.97) * mm, "end": v(621.26, 33.21) * mm});
            skLineSegment(sketch, "E1080.MirrorCS", {"start": v(613.2, 33.2) * mm, "end": v(613.2, 32.43) * mm});
            skLineSegment(sketch, "E1081.MirrorCS", {"start": v(591.58, 33.9) * mm, "end": v(591.58, 33.14) * mm});
            skLineSegment(sketch, "E1082.MirrorCS", {"start": v(581.75, 33.88) * mm, "end": v(591.58, 33.9) * mm});
            skLineSegment(sketch, "E1083.MirrorCS", {"start": v(564.62, 33.84) * mm, "end": v(575.4, 33.86) * mm});
            skLineSegment(sketch, "E1084.MirrorCS", {"start": v(564.62, 32.31) * mm, "end": v(575.4, 32.34) * mm});
            skLineSegment(sketch, "E1085.MirrorCS", {"start": v(613.2, 33.96) * mm, "end": v(621.26, 33.97) * mm});
            skLineSegment(sketch, "E1086.MirrorCS", {"start": v(597.93, 33.92) * mm, "end": v(606.85, 33.94) * mm});
            skLineSegment(sketch, "E1087.MirrorCS", {"start": v(581.76, 32.36) * mm, "end": v(591.58, 32.38) * mm});
            skLineSegment(sketch, "E1088.MirrorCS", {"start": v(597.93, 32.4) * mm, "end": v(606.85, 32.42) * mm});
            skLineSegment(sketch, "E1089.MirrorCS", {"start": v(613.2, 32.43) * mm, "end": v(621.26, 32.45) * mm});
            skLineSegment(sketch, "E1090.MirrorCS", {"start": v(378.92, 31.87) * mm, "end": v(378.92, 32.63) * mm});
            skSolve(sketch);
        }
        {
            var Q0;
            Q0=qCreatedBy(makeId("Front.planeOp"),FACE);
            var sketch = newSketch(context, id + "F1", { "sketchPlane" : qUnion([Q0])});
            skLineSegment(sketch, "E1091", {"start": v(0, 0) * mm, "end": v(0, 56.39) * mm});
            skLineSegment(sketch, "E1092", {"start": v(0, 56.39) * mm, "end": v(635, 68.83) * mm});
            skLineSegment(sketch, "E1093", {"start": v(635, 68.83) * mm, "end": v(635, -12.45) * mm});
            skLineSegment(sketch, "E1094", {"start": v(635, -12.45) * mm, "end": v(0, 0) * mm});
            skLineSegment(sketch, "E1095", {"start": v(0, 28.2) * mm, "end": v(897.35, 28.2) * mm, "construction": true});
            skSolve(sketch);
        }
        {
            var Q0;
            Q0=qSketchRegion(id+"F1",true);
            extrude(context, id + "F2", {"entities" : qUnion([Q0]), "depth" : 1.52 * mm});
        }
        {
            var Q0;
            Q0=makeQuery(id+"F2.opExtrude","CAP_FACE",FACE,{"disambiguationData":[OSD([sQuery(id+"F1.wireOp",EDGE,"E1091"),sQuery(id+"F1.wireOp",EDGE,"E1092"),sQuery(id+"F1.wireOp",EDGE,"E1093"),sQuery(id+"F1.wireOp",EDGE,"E1094")])],"isStart":false});
            var sketch = newSketch(context, id + "F3", { "sketchPlane" : qUnion([Q0])});
            skLineSegment(sketch, "E1096", {"start": v(0, 28.2) * mm, "end": v(635, 28.2) * mm, "construction": true});
            skSolve(sketch);
        }
        {
            var Q0;
            Q0=qSketchRegion(id+"F0",true);
            extrude(context, id + "F4", {"entities" : qUnion([Q0]), "operationType" : NewBodyOperationType.REMOVE, "endBound" : BoundingType.THROUGH_ALL, "depth" : 25.4 * mm});
        }
        {
            var Q0;
            Q0=makeQuery(id+"F3.imprint","IMPRINT",FACE,{"disambiguationData":[TD([[makeQuery(id+"F3.imprint","IMPRINT",EDGE,{"derivedFrom":makeQuery(id+"F2.opExtrude","CAP_EDGE",EDGE,{"disambiguationData":[OSD([sQuery(id+"F1.wireOp",EDGE,"E1091")])],"isStart":false})}),-1.0]])]});
            var sketch = newSketch(context, id + "F5", { "sketchPlane" : qUnion([Q0])});
            skCircle(sketch, "E1097", {"center": v(97.4, 13.14) * mm, "radius": 1.13 * mm});
            skLineSegment(sketch, "E1098", {"start": v(0, 14.1) * mm, "end": v(635, 7.87) * mm, "construction": true});
            skCircle(sketch, "E1099", {"center": v(3.18, 14.07) * mm, "radius": 1.13 * mm});
            skCircle(sketch, "E1100", {"center": v(181.33, 12.32) * mm, "radius": 1.13 * mm});
            skCircle(sketch, "E1101", {"center": v(290.4, 11.25) * mm, "radius": 1.13 * mm});
            skCircle(sketch, "E1102", {"center": v(409.3, 10.09) * mm, "radius": 1.13 * mm});
            skCircle(sketch, "E1103", {"center": v(524.06, 8.96) * mm, "radius": 1.13 * mm});
            skCircle(sketch, "E1104", {"center": v(624.44, 7.98) * mm, "radius": 1.13 * mm});
            skCircle(sketch, "E1105.MirrorC", {"center": v(97.4, 43.25) * mm, "radius": 1.13 * mm});
            skCircle(sketch, "E1106.MirrorC", {"center": v(3.18, 42.32) * mm, "radius": 1.13 * mm});
            skCircle(sketch, "E1107.MirrorC", {"center": v(181.33, 44.07) * mm, "radius": 1.13 * mm});
            skCircle(sketch, "E1108.MirrorC", {"center": v(290.4, 45.14) * mm, "radius": 1.13 * mm});
            skCircle(sketch, "E1109.MirrorC", {"center": v(409.3, 46.3) * mm, "radius": 1.13 * mm});
            skCircle(sketch, "E1110.MirrorC", {"center": v(524.06, 47.43) * mm, "radius": 1.13 * mm});
            skCircle(sketch, "E1111.MirrorC", {"center": v(624.44, 48.41) * mm, "radius": 1.13 * mm});
            skSolve(sketch);
        }
        {
            var Q0;
            Q0 = qSketchRegion(id + "F5", true);
            extrude(context, id + "F6", {"entities" : qUnion([Q0]), "operationType" : NewBodyOperationType.REMOVE, "endBound" : BoundingType.THROUGH_ALL, "depth" : 25.4 * mm});
        }
        {
            var Q0;
            Q0 = qSketchRegion(id + "F5", true);
            extrude(context, id + "F7", {"entities" : qUnion([Q0]), "operationType" : NewBodyOperationType.REMOVE, "endBound" : BoundingType.THROUGH_ALL, "oppositeDirection" : true, "depth" : 25.4 * mm});
        }
    });
